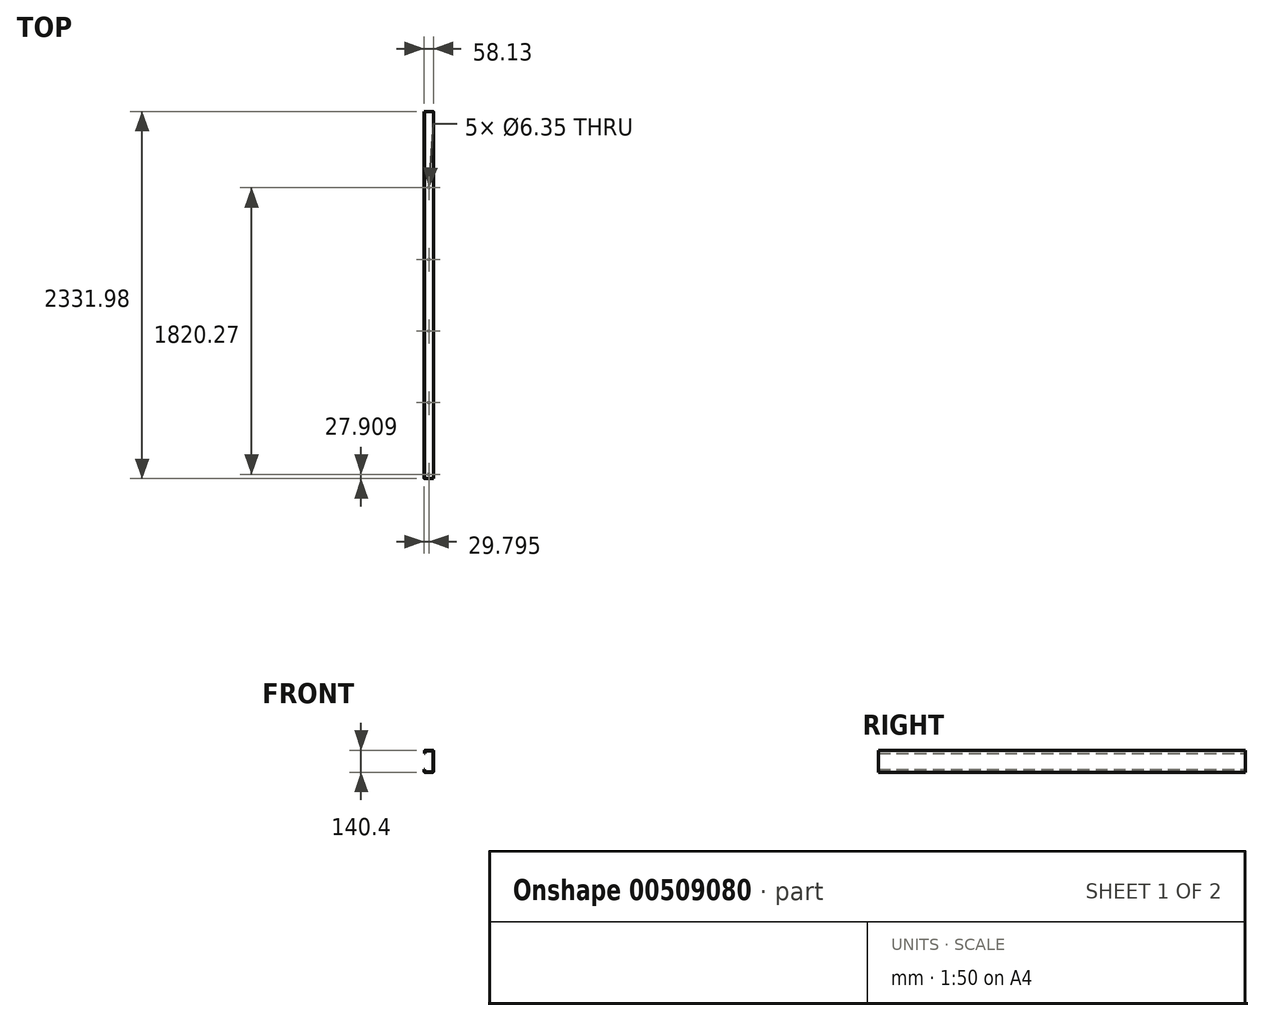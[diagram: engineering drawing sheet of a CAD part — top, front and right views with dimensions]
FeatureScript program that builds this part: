
annotation { "Feature Type Name" : "Feature", "Feature Type Description" : "" }
export const myFeature = defineFeature(function(context is Context, id is Id, definition is map)
    precondition{}
    {
        {
            var Q0;
            Q0=qCreatedBy(makeId("Front.planeOp"),FACE);
            var sketch = newSketch(context, id + "F0", { "sketchPlane" : qUnion([Q0])});
            skLineSegment(sketch, "E0", {"start": v(-431.8, -558.8) * mm, "end": v(431.8, -558.8) * mm});
            skLineSegment(sketch, "E1", {"start": v(431.8, -558.8) * mm, "end": v(431.8, 558.8) * mm});
            skLineSegment(sketch, "E2", {"start": v(431.8, 558.8) * mm, "end": v(-431.8, 558.8) * mm});
            skLineSegment(sketch, "E3", {"start": v(-431.8, 558.8) * mm, "end": v(-431.8, -558.8) * mm});
            skLineSegment(sketch, "E4", {"start": v(-381, -504.83) * mm, "end": v(381, -504.83) * mm});
            skLineSegment(sketch, "E5", {"start": v(381, -504.83) * mm, "end": v(381, 504.83) * mm});
            skLineSegment(sketch, "E6", {"start": v(381, 504.83) * mm, "end": v(360.7, 504.83) * mm});
            skLineSegment(sketch, "E7", {"start": v(265.82, 504.83) * mm, "end": v(-381, 504.83) * mm});
            skLineSegment(sketch, "E8", {"start": v(-381, 504.83) * mm, "end": v(-381, -504.83) * mm});
            skLineSegment(sketch, "E9", {"start": v(-381, -403.23) * mm, "end": v(381, -403.23) * mm});
            skLineSegment(sketch, "E10", {"start": v(-152.4, -403.23) * mm, "end": v(-152.4, -504.83) * mm});
            skLineSegment(sketch, "E11", {"start": v(152.4, -403.23) * mm, "end": v(152.4, -504.83) * mm});
            skLineSegment(sketch, "E12", {"start": v(349.12, 503.33) * mm, "end": v(324.77, 544.8) * mm});
            skLineSegment(sketch, "E13", {"start": v(324.92, 525.17) * mm, "end": v(343.26, 493.25) * mm});
            skLineSegment(sketch, "E14", {"start": v(345.3, 496.77) * mm, "end": v(323.11, 534.57) * mm});
            skLineSegment(sketch, "E15", {"start": v(351.17, 506.85) * mm, "end": v(327.06, 548.5) * mm});
            skLineSegment(sketch, "E16", {"start": v(335.24, 486.66) * mm, "end": v(339.43, 486.66) * mm});
            skLineSegment(sketch, "E17", {"start": v(323.53, 514.34) * mm, "end": v(339.43, 486.66) * mm});
            skLineSegment(sketch, "E18", {"start": v(324.77, 544.8) * mm, "end": v(303.2, 507.27) * mm});
            skLineSegment(sketch, "E19", {"start": v(323.11, 534.57) * mm, "end": v(305.2, 503.47) * mm});
            skLineSegment(sketch, "E20", {"start": v(303.02, 548.5) * mm, "end": v(279.32, 507.27) * mm});
            skLineSegment(sketch, "E21", {"start": v(305.2, 503.47) * mm, "end": v(281.51, 503.47) * mm});
            skLineSegment(sketch, "E22", {"start": v(303.2, 507.27) * mm, "end": v(279.32, 507.27) * mm});
            skLineSegment(sketch, "E23", {"start": v(287.46, 493.17) * mm, "end": v(311.53, 493.17) * mm});
            skLineSegment(sketch, "E24", {"start": v(285.48, 496.6) * mm, "end": v(309, 496.6) * mm});
            skLineSegment(sketch, "E25", {"start": v(315.3, 486.66) * mm, "end": v(291.22, 486.66) * mm});
            skLineSegment(sketch, "E26", {"start": v(281.51, 503.47) * mm, "end": v(285.48, 496.6) * mm});
            skLineSegment(sketch, "E27", {"start": v(287.46, 493.17) * mm, "end": v(291.22, 486.66) * mm});
            skLineSegment(sketch, "E28", {"start": v(309, 496.6) * mm, "end": v(324.92, 525.17) * mm});
            skLineSegment(sketch, "E29", {"start": v(311.53, 493.17) * mm, "end": v(323.53, 514.34) * mm});
            skLineSegment(sketch, "E30", {"start": v(325.28, 503.65) * mm, "end": v(315.3, 486.66) * mm});
            skLineSegment(sketch, "E31", {"start": v(319.7, 486.66) * mm, "end": v(326.89, 486.66) * mm});
            skLineSegment(sketch, "E32", {"start": v(319.7, 486.66) * mm, "end": v(323.3, 492.99) * mm});
            skLineSegment(sketch, "E33", {"start": v(335.24, 486.66) * mm, "end": v(325.28, 503.65) * mm});
            skLineSegment(sketch, "E34", {"start": v(323.3, 492.99) * mm, "end": v(326.89, 486.66) * mm});
            skLineSegment(sketch, "E35", {"start": v(327.06, 548.5) * mm, "end": v(303.02, 548.5) * mm});
            skLineSegment(sketch, "E36", {"start": v(343.26, 493.25) * mm, "end": v(345.3, 496.77) * mm});
            skLineSegment(sketch, "E37", {"start": v(349.12, 503.33) * mm, "end": v(351.17, 506.85) * mm});
            skCircle(sketch, "E38", {"center": v(350.6, 458.79) * mm, "radius": 1.85 * mm});
            skLineSegment(sketch, "E39", {"start": v(-201.65, 389.86) * mm, "end": v(-204.7, 389.86) * mm});
            skLineSegment(sketch, "E40", {"start": v(-201.65, 287.56) * mm, "end": v(-204.7, 287.56) * mm});
            skLineSegment(sketch, "E41", {"start": v(-204.7, 389.86) * mm, "end": v(-204.7, 405.1) * mm});
            skLineSegment(sketch, "E42", {"start": v(-201.65, 389.86) * mm, "end": v(-201.65, 405.1) * mm});
            skArc(sketch, "E43", {"start": v(-200.89, 405.86) * mm, "mid": v(-201.43, 405.64) * mm, "end": v(-201.65, 405.1) * mm});
            skArc(sketch, "E44", {"start": v(-200.89, 408.9) * mm, "mid": v(-203.58, 407.8) * mm, "end": v(-204.7, 405.1) * mm});
            skLineSegment(sketch, "E45", {"start": v(-200.89, 408.9) * mm, "end": v(-151.83, 408.9) * mm});
            skLineSegment(sketch, "E46", {"start": v(-200.89, 405.86) * mm, "end": v(-151.83, 405.86) * mm});
            skArc(sketch, "E47", {"start": v(-151.07, 405.1) * mm, "mid": v(-151.3, 405.64) * mm, "end": v(-151.83, 405.86) * mm});
            skArc(sketch, "E48", {"start": v(-148.02, 405.1) * mm, "mid": v(-149.14, 407.8) * mm, "end": v(-151.83, 408.9) * mm});
            skLineSegment(sketch, "E49", {"start": v(-148.02, 405.1) * mm, "end": v(-148.02, 272.32) * mm});
            skLineSegment(sketch, "E50", {"start": v(-151.07, 405.1) * mm, "end": v(-151.07, 272.32) * mm});
            skLineSegment(sketch, "E51", {"start": v(-204.7, 287.56) * mm, "end": v(-204.7, 273.15) * mm});
            skLineSegment(sketch, "E52", {"start": v(-201.65, 287.56) * mm, "end": v(-201.65, 273.15) * mm});
            skLineSegment(sketch, "E53", {"start": v(-200.06, 268.51) * mm, "end": v(-151.83, 268.51) * mm});
            skLineSegment(sketch, "E54", {"start": v(-200.06, 271.56) * mm, "end": v(-151.83, 271.56) * mm});
            skArc(sketch, "E55", {"start": v(-151.83, 271.56) * mm, "mid": v(-151.3, 271.79) * mm, "end": v(-151.07, 272.32) * mm});
            skArc(sketch, "E56", {"start": v(-151.83, 268.51) * mm, "mid": v(-149.14, 269.63) * mm, "end": v(-148.02, 272.32) * mm});
            skArc(sketch, "E57", {"start": v(-201.65, 273.15) * mm, "mid": v(-201.19, 272.03) * mm, "end": v(-200.06, 271.56) * mm});
            skArc(sketch, "E58", {"start": v(-204.7, 273.15) * mm, "mid": v(-203.34, 269.87) * mm, "end": v(-200.06, 268.51) * mm});
            skLineSegment(sketch, "E59", {"start": v(268.24, 192.18) * mm, "end": v(-275.4, 192.18) * mm});
            skLineSegment(sketch, "E60", {"start": v(-275.4, 267.58) * mm, "end": v(268.24, 267.58) * mm});
            skLineSegment(sketch, "E61", {"start": v(-275.4, 191.38) * mm, "end": v(268.24, 191.38) * mm});
            skLineSegment(sketch, "E62", {"start": v(-275.4, 189.56) * mm, "end": v(-275.4, 233.5) * mm});
            skLineSegment(sketch, "E63", {"start": v(-275.4, 238.46) * mm, "end": v(-275.4, 270.12) * mm});
            skLineSegment(sketch, "E64", {"start": v(-275.4, 233.5) * mm, "end": v(-264.27, 236) * mm});
            skLineSegment(sketch, "E65", {"start": v(-287.59, 236) * mm, "end": v(-275.4, 238.46) * mm});
            skLineSegment(sketch, "E66", {"start": v(-287.59, 236) * mm, "end": v(-264.27, 236) * mm});
            skLineSegment(sketch, "E67", {"start": v(268.24, 189.56) * mm, "end": v(268.24, 233.5) * mm});
            skLineSegment(sketch, "E68", {"start": v(268.24, 238.46) * mm, "end": v(268.24, 270.12) * mm});
            skLineSegment(sketch, "E69", {"start": v(268.24, 233.5) * mm, "end": v(279.38, 236) * mm});
            skLineSegment(sketch, "E70", {"start": v(256.06, 236) * mm, "end": v(268.24, 238.46) * mm});
            skLineSegment(sketch, "E71", {"start": v(256.06, 236) * mm, "end": v(279.38, 236) * mm});
            skLineSegment(sketch, "E72", {"start": v(267.92, 175.66) * mm, "end": v(267.92, 187.92) * mm});
            skLineSegment(sketch, "E73", {"start": v(-275.4, 175.66) * mm, "end": v(-275.4, 187.92) * mm});
            skLineSegment(sketch, "E74", {"start": v(131.2, 389.86) * mm, "end": v(128.15, 389.86) * mm});
            skLineSegment(sketch, "E75", {"start": v(131.2, 287.54) * mm, "end": v(128.15, 287.54) * mm});
            skLineSegment(sketch, "E76", {"start": v(128.15, 389.86) * mm, "end": v(128.15, 405.1) * mm});
            skLineSegment(sketch, "E77", {"start": v(131.2, 389.86) * mm, "end": v(131.2, 405.1) * mm});
            skArc(sketch, "E78", {"start": v(131.96, 408.9) * mm, "mid": v(129.27, 407.8) * mm, "end": v(128.15, 405.1) * mm});
            skLineSegment(sketch, "E79", {"start": v(131.96, 408.9) * mm, "end": v(182.96, 408.9) * mm});
            skLineSegment(sketch, "E80", {"start": v(131.96, 405.86) * mm, "end": v(182.96, 405.86) * mm});
            skArc(sketch, "E81", {"start": v(183.72, 405.1) * mm, "mid": v(183.5, 405.64) * mm, "end": v(182.96, 405.86) * mm});
            skArc(sketch, "E82", {"start": v(186.77, 405.1) * mm, "mid": v(185.65, 407.8) * mm, "end": v(182.96, 408.9) * mm});
            skLineSegment(sketch, "E83", {"start": v(186.77, 405.1) * mm, "end": v(186.77, 272.3) * mm});
            skLineSegment(sketch, "E84", {"start": v(183.72, 405.1) * mm, "end": v(183.72, 272.3) * mm});
            skLineSegment(sketch, "E85", {"start": v(128.15, 287.54) * mm, "end": v(128.15, 273.12) * mm});
            skLineSegment(sketch, "E86", {"start": v(131.2, 287.54) * mm, "end": v(131.2, 273.12) * mm});
            skLineSegment(sketch, "E87", {"start": v(132.79, 268.49) * mm, "end": v(182.96, 268.49) * mm});
            skLineSegment(sketch, "E88", {"start": v(132.79, 271.53) * mm, "end": v(182.96, 271.53) * mm});
            skArc(sketch, "E89", {"start": v(182.96, 271.53) * mm, "mid": v(183.5, 271.76) * mm, "end": v(183.72, 272.3) * mm});
            skArc(sketch, "E90", {"start": v(182.96, 268.49) * mm, "mid": v(185.65, 269.6) * mm, "end": v(186.77, 272.3) * mm});
            skArc(sketch, "E91", {"start": v(131.2, 273.12) * mm, "mid": v(131.67, 272) * mm, "end": v(132.79, 271.53) * mm});
            skArc(sketch, "E92", {"start": v(128.15, 273.12) * mm, "mid": v(129.51, 269.84) * mm, "end": v(132.79, 268.49) * mm});
            skLineSegment(sketch, "E93", {"start": v(-275.4, 266.78) * mm, "end": v(268.24, 266.78) * mm});
            skArc(sketch, "E94", {"start": v(131.96, 405.86) * mm, "mid": v(131.42, 405.64) * mm, "end": v(131.2, 405.1) * mm});
            skLineSegment(sketch, "E95", {"start": v(-148.02, 350.55) * mm, "end": v(-147.38, 350.55) * mm});
            skLineSegment(sketch, "E96", {"start": v(268.24, 220.63) * mm, "end": v(-275.4, 220.63) * mm});
            skLineSegment(sketch, "E97", {"start": v(-275.4, 219.83) * mm, "end": v(268.24, 219.83) * mm});
            skLineSegment(sketch, "E98", {"start": v(111.4, 219.88) * mm, "end": v(200.2, 219.88) * mm});
            skLineSegment(sketch, "E99", {"start": v(200.2, 219.88) * mm, "end": v(200.2, 218.1) * mm});
            skLineSegment(sketch, "E100", {"start": v(111.4, 219.88) * mm, "end": v(111.4, 218.1) * mm});
            skLineSegment(sketch, "E101", {"start": v(111.4, 218.1) * mm, "end": v(200.2, 218.1) * mm});
            skLineSegment(sketch, "E102", {"start": v(165.87, 216.24) * mm, "end": v(165.87, 217.5) * mm});
            skLineSegment(sketch, "E103", {"start": v(152.66, 216.24) * mm, "end": v(152.66, 217.5) * mm});
            skLineSegment(sketch, "E104", {"start": v(164.46, 211.81) * mm, "end": v(164.46, 216.24) * mm});
            skLineSegment(sketch, "E105", {"start": v(154.07, 211.81) * mm, "end": v(154.07, 216.24) * mm});
            skLineSegment(sketch, "E106", {"start": v(161.7, 259.32) * mm, "end": v(161.7, 260.34) * mm});
            skLineSegment(sketch, "E107", {"start": v(161.7, 261.14) * mm, "end": v(161.7, 262.16) * mm});
            skLineSegment(sketch, "E108", {"start": v(161.7, 262.95) * mm, "end": v(161.7, 263.97) * mm});
            skLineSegment(sketch, "E109", {"start": v(161.7, 264.76) * mm, "end": v(161.7, 265.78) * mm});
            skLineSegment(sketch, "E110", {"start": v(161.7, 266.58) * mm, "end": v(161.7, 267.6) * mm});
            skLineSegment(sketch, "E111", {"start": v(161.7, 268.39) * mm, "end": v(161.7, 269.41) * mm});
            skLineSegment(sketch, "E112", {"start": v(161.7, 270.2) * mm, "end": v(161.7, 271.22) * mm});
            skLineSegment(sketch, "E113", {"start": v(161.7, 272.02) * mm, "end": v(161.7, 273.04) * mm});
            skLineSegment(sketch, "E114", {"start": v(161.7, 273.83) * mm, "end": v(161.7, 274.85) * mm});
            skLineSegment(sketch, "E115", {"start": v(161.7, 275.64) * mm, "end": v(161.7, 276.67) * mm});
            skLineSegment(sketch, "E116", {"start": v(161.7, 277.46) * mm, "end": v(161.7, 278.48) * mm});
            skLineSegment(sketch, "E117", {"start": v(156.83, 257.5) * mm, "end": v(156.83, 258.53) * mm});
            skLineSegment(sketch, "E118", {"start": v(156.83, 259.32) * mm, "end": v(156.83, 260.34) * mm});
            skLineSegment(sketch, "E119", {"start": v(156.83, 261.14) * mm, "end": v(156.83, 262.16) * mm});
            skLineSegment(sketch, "E120", {"start": v(156.83, 262.95) * mm, "end": v(156.83, 263.97) * mm});
            skLineSegment(sketch, "E121", {"start": v(156.83, 264.76) * mm, "end": v(156.83, 265.78) * mm});
            skLineSegment(sketch, "E122", {"start": v(156.83, 266.58) * mm, "end": v(156.83, 267.6) * mm});
            skLineSegment(sketch, "E123", {"start": v(156.83, 268.39) * mm, "end": v(156.83, 269.41) * mm});
            skLineSegment(sketch, "E124", {"start": v(156.83, 270.2) * mm, "end": v(156.83, 271.22) * mm});
            skLineSegment(sketch, "E125", {"start": v(156.83, 272.02) * mm, "end": v(156.83, 273.04) * mm});
            skLineSegment(sketch, "E126", {"start": v(156.83, 273.83) * mm, "end": v(156.83, 274.85) * mm});
            skLineSegment(sketch, "E127", {"start": v(156.83, 275.64) * mm, "end": v(156.83, 276.67) * mm});
            skLineSegment(sketch, "E128", {"start": v(156.14, 258.93) * mm, "end": v(156.83, 258.53) * mm});
            skLineSegment(sketch, "E129", {"start": v(156.14, 258.93) * mm, "end": v(156.83, 259.32) * mm});
            skLineSegment(sketch, "E130", {"start": v(156.14, 260.74) * mm, "end": v(156.83, 260.34) * mm});
            skLineSegment(sketch, "E131", {"start": v(156.14, 260.74) * mm, "end": v(156.83, 261.14) * mm});
            skLineSegment(sketch, "E132", {"start": v(162.39, 260.74) * mm, "end": v(161.7, 260.34) * mm});
            skLineSegment(sketch, "E133", {"start": v(162.39, 260.74) * mm, "end": v(161.7, 261.14) * mm});
            skLineSegment(sketch, "E134", {"start": v(162.39, 262.55) * mm, "end": v(161.7, 262.16) * mm});
            skLineSegment(sketch, "E135", {"start": v(162.39, 262.55) * mm, "end": v(161.7, 262.95) * mm});
            skLineSegment(sketch, "E136", {"start": v(156.14, 258.93) * mm, "end": v(162.39, 260.74) * mm});
            skLineSegment(sketch, "E137", {"start": v(156.14, 260.74) * mm, "end": v(162.39, 262.55) * mm});
            skLineSegment(sketch, "E138", {"start": v(156.83, 258.53) * mm, "end": v(161.7, 260.34) * mm});
            skLineSegment(sketch, "E139", {"start": v(156.83, 259.32) * mm, "end": v(161.7, 261.14) * mm});
            skLineSegment(sketch, "E140", {"start": v(156.83, 260.34) * mm, "end": v(161.7, 262.16) * mm});
            skLineSegment(sketch, "E141", {"start": v(156.83, 261.14) * mm, "end": v(161.7, 262.95) * mm});
            skLineSegment(sketch, "E142", {"start": v(156.14, 262.55) * mm, "end": v(156.83, 262.16) * mm});
            skLineSegment(sketch, "E143", {"start": v(156.14, 262.55) * mm, "end": v(156.83, 262.95) * mm});
            skLineSegment(sketch, "E144", {"start": v(156.14, 264.37) * mm, "end": v(156.83, 263.97) * mm});
            skLineSegment(sketch, "E145", {"start": v(156.14, 264.37) * mm, "end": v(156.83, 264.76) * mm});
            skLineSegment(sketch, "E146", {"start": v(162.39, 264.37) * mm, "end": v(161.7, 263.97) * mm});
            skLineSegment(sketch, "E147", {"start": v(162.39, 264.37) * mm, "end": v(161.7, 264.76) * mm});
            skLineSegment(sketch, "E148", {"start": v(162.39, 266.18) * mm, "end": v(161.7, 265.78) * mm});
            skLineSegment(sketch, "E149", {"start": v(162.39, 266.18) * mm, "end": v(161.7, 266.58) * mm});
            skLineSegment(sketch, "E150", {"start": v(156.14, 262.55) * mm, "end": v(162.39, 264.37) * mm});
            skLineSegment(sketch, "E151", {"start": v(156.14, 264.37) * mm, "end": v(162.39, 266.18) * mm});
            skLineSegment(sketch, "E152", {"start": v(156.83, 262.16) * mm, "end": v(161.7, 263.97) * mm});
            skLineSegment(sketch, "E153", {"start": v(156.83, 262.95) * mm, "end": v(161.7, 264.76) * mm});
            skLineSegment(sketch, "E154", {"start": v(156.83, 263.97) * mm, "end": v(161.7, 265.78) * mm});
            skLineSegment(sketch, "E155", {"start": v(156.83, 264.76) * mm, "end": v(161.7, 266.58) * mm});
            skLineSegment(sketch, "E156", {"start": v(156.14, 266.18) * mm, "end": v(156.83, 265.78) * mm});
            skLineSegment(sketch, "E157", {"start": v(156.14, 266.18) * mm, "end": v(156.83, 266.58) * mm});
            skLineSegment(sketch, "E158", {"start": v(162.39, 268) * mm, "end": v(161.7, 267.6) * mm});
            skLineSegment(sketch, "E159", {"start": v(162.39, 268) * mm, "end": v(161.7, 268.39) * mm});
            skLineSegment(sketch, "E160", {"start": v(156.14, 266.18) * mm, "end": v(162.39, 268) * mm});
            skLineSegment(sketch, "E161", {"start": v(156.83, 265.78) * mm, "end": v(161.7, 267.6) * mm});
            skLineSegment(sketch, "E162", {"start": v(156.83, 266.58) * mm, "end": v(161.7, 268.39) * mm});
            skLineSegment(sketch, "E163", {"start": v(156.14, 268) * mm, "end": v(156.83, 267.6) * mm});
            skLineSegment(sketch, "E164", {"start": v(156.14, 268) * mm, "end": v(156.83, 268.39) * mm});
            skLineSegment(sketch, "E165", {"start": v(156.14, 269.8) * mm, "end": v(156.83, 269.41) * mm});
            skLineSegment(sketch, "E166", {"start": v(156.14, 269.8) * mm, "end": v(156.83, 270.2) * mm});
            skLineSegment(sketch, "E167", {"start": v(162.39, 269.8) * mm, "end": v(161.7, 269.41) * mm});
            skLineSegment(sketch, "E168", {"start": v(162.39, 269.8) * mm, "end": v(161.7, 270.2) * mm});
            skLineSegment(sketch, "E169", {"start": v(162.39, 271.62) * mm, "end": v(161.7, 271.22) * mm});
            skLineSegment(sketch, "E170", {"start": v(162.39, 271.62) * mm, "end": v(161.7, 272.02) * mm});
            skLineSegment(sketch, "E171", {"start": v(156.14, 268) * mm, "end": v(162.39, 269.8) * mm});
            skLineSegment(sketch, "E172", {"start": v(156.14, 269.8) * mm, "end": v(162.39, 271.62) * mm});
            skLineSegment(sketch, "E173", {"start": v(156.83, 267.6) * mm, "end": v(161.7, 269.41) * mm});
            skLineSegment(sketch, "E174", {"start": v(156.83, 268.39) * mm, "end": v(161.7, 270.2) * mm});
            skLineSegment(sketch, "E175", {"start": v(156.83, 269.41) * mm, "end": v(161.7, 271.22) * mm});
            skLineSegment(sketch, "E176", {"start": v(156.83, 270.2) * mm, "end": v(161.7, 272.02) * mm});
            skLineSegment(sketch, "E177", {"start": v(156.14, 271.62) * mm, "end": v(156.83, 271.22) * mm});
            skLineSegment(sketch, "E178", {"start": v(156.14, 271.62) * mm, "end": v(156.83, 272.02) * mm});
            skLineSegment(sketch, "E179", {"start": v(156.14, 273.43) * mm, "end": v(156.83, 273.04) * mm});
            skLineSegment(sketch, "E180", {"start": v(156.14, 273.43) * mm, "end": v(156.83, 273.83) * mm});
            skLineSegment(sketch, "E181", {"start": v(162.39, 273.43) * mm, "end": v(161.7, 273.04) * mm});
            skLineSegment(sketch, "E182", {"start": v(162.39, 273.43) * mm, "end": v(161.7, 273.83) * mm});
            skLineSegment(sketch, "E183", {"start": v(162.39, 275.25) * mm, "end": v(161.7, 274.85) * mm});
            skLineSegment(sketch, "E184", {"start": v(162.39, 275.25) * mm, "end": v(161.7, 275.64) * mm});
            skLineSegment(sketch, "E185", {"start": v(156.14, 271.62) * mm, "end": v(162.39, 273.43) * mm});
            skLineSegment(sketch, "E186", {"start": v(156.14, 273.43) * mm, "end": v(162.39, 275.25) * mm});
            skLineSegment(sketch, "E187", {"start": v(156.83, 271.22) * mm, "end": v(161.7, 273.04) * mm});
            skLineSegment(sketch, "E188", {"start": v(156.83, 272.02) * mm, "end": v(161.7, 273.83) * mm});
            skLineSegment(sketch, "E189", {"start": v(156.83, 273.04) * mm, "end": v(161.7, 274.85) * mm});
            skLineSegment(sketch, "E190", {"start": v(156.83, 273.83) * mm, "end": v(161.7, 275.64) * mm});
            skLineSegment(sketch, "E191", {"start": v(156.14, 275.25) * mm, "end": v(156.83, 274.85) * mm});
            skLineSegment(sketch, "E192", {"start": v(156.14, 275.25) * mm, "end": v(156.83, 275.64) * mm});
            skLineSegment(sketch, "E193", {"start": v(156.14, 277.06) * mm, "end": v(156.83, 276.67) * mm});
            skLineSegment(sketch, "E194", {"start": v(156.14, 277.06) * mm, "end": v(156.83, 277.46) * mm});
            skLineSegment(sketch, "E195", {"start": v(162.39, 277.06) * mm, "end": v(161.7, 276.67) * mm});
            skLineSegment(sketch, "E196", {"start": v(162.39, 277.06) * mm, "end": v(161.7, 277.46) * mm});
            skLineSegment(sketch, "E197", {"start": v(162.39, 278.87) * mm, "end": v(161.7, 278.48) * mm});
            skLineSegment(sketch, "E198", {"start": v(162.39, 278.87) * mm, "end": v(161.7, 279.27) * mm});
            skLineSegment(sketch, "E199", {"start": v(156.14, 275.25) * mm, "end": v(162.39, 277.06) * mm});
            skLineSegment(sketch, "E200", {"start": v(156.14, 277.06) * mm, "end": v(162.39, 278.87) * mm});
            skLineSegment(sketch, "E201", {"start": v(156.83, 274.85) * mm, "end": v(161.7, 276.67) * mm});
            skLineSegment(sketch, "E202", {"start": v(156.83, 275.64) * mm, "end": v(161.7, 277.46) * mm});
            skLineSegment(sketch, "E203", {"start": v(156.83, 276.67) * mm, "end": v(161.7, 278.48) * mm});
            skLineSegment(sketch, "E204", {"start": v(156.83, 277.46) * mm, "end": v(161.7, 279.27) * mm});
            skLineSegment(sketch, "E205", {"start": v(152.66, 217.5) * mm, "end": v(165.87, 217.5) * mm});
            skLineSegment(sketch, "E206", {"start": v(152.66, 216.24) * mm, "end": v(165.87, 216.24) * mm});
            skLineSegment(sketch, "E207", {"start": v(154.77, 211.41) * mm, "end": v(163.76, 211.41) * mm});
            skLineSegment(sketch, "E208", {"start": v(156.67, 211.81) * mm, "end": v(156.67, 216.24) * mm});
            skLineSegment(sketch, "E209", {"start": v(161.86, 211.81) * mm, "end": v(161.86, 216.24) * mm});
            skLineSegment(sketch, "E210", {"start": v(154.77, 211.41) * mm, "end": v(154.07, 211.81) * mm});
            skLineSegment(sketch, "E211", {"start": v(163.76, 211.41) * mm, "end": v(164.46, 211.81) * mm});
            skLineSegment(sketch, "E212", {"start": v(161.16, 211.41) * mm, "end": v(161.86, 211.81) * mm});
            skLineSegment(sketch, "E213", {"start": v(155.97, 211.41) * mm, "end": v(156.67, 211.81) * mm});
            skLineSegment(sketch, "E214", {"start": v(162.56, 211.41) * mm, "end": v(161.86, 211.81) * mm});
            skLineSegment(sketch, "E215", {"start": v(157.36, 211.41) * mm, "end": v(156.67, 211.81) * mm});
            skLineSegment(sketch, "E216", {"start": v(156.83, 277.46) * mm, "end": v(156.83, 288.94) * mm});
            skLineSegment(sketch, "E217", {"start": v(161.05, 279.03) * mm, "end": v(161.05, 288.94) * mm});
            skLineSegment(sketch, "E218", {"start": v(158.94, 290.16) * mm, "end": v(156.83, 288.94) * mm});
            skLineSegment(sketch, "E219", {"start": v(158.94, 290.16) * mm, "end": v(161.05, 288.94) * mm});
            skLineSegment(sketch, "E220", {"start": v(158.94, 290.16) * mm, "end": v(158.94, 280.63) * mm});
            skArc(sketch, "E221", {"start": v(158.94, 280.63) * mm, "mid": v(159.28, 279.49) * mm, "end": v(160.18, 278.7) * mm});
            skLineSegment(sketch, "E222", {"start": v(156.14, 257.11) * mm, "end": v(156.83, 256.72) * mm});
            skLineSegment(sketch, "E223", {"start": v(156.14, 257.11) * mm, "end": v(156.83, 257.5) * mm});
            skLineSegment(sketch, "E224", {"start": v(162.39, 258.93) * mm, "end": v(161.7, 258.53) * mm});
            skLineSegment(sketch, "E225", {"start": v(162.39, 258.93) * mm, "end": v(161.7, 259.32) * mm});
            skLineSegment(sketch, "E226", {"start": v(156.14, 257.11) * mm, "end": v(162.39, 258.93) * mm});
            skLineSegment(sketch, "E227", {"start": v(156.83, 256.72) * mm, "end": v(161.7, 258.53) * mm});
            skLineSegment(sketch, "E228", {"start": v(156.83, 257.5) * mm, "end": v(161.7, 259.32) * mm});
            skLineSegment(sketch, "E229", {"start": v(156.83, 256.72) * mm, "end": v(156.83, 217.5) * mm});
            skLineSegment(sketch, "E230", {"start": v(161.7, 258.53) * mm, "end": v(161.7, 217.5) * mm});
            skLineSegment(sketch, "E231", {"start": v(-224.84, 219.88) * mm, "end": v(-136.05, 219.88) * mm});
            skLineSegment(sketch, "E232", {"start": v(-224.84, 218.1) * mm, "end": v(-136.05, 218.1) * mm});
            skLineSegment(sketch, "E233", {"start": v(-136.05, 219.88) * mm, "end": v(-136.05, 218.1) * mm});
            skLineSegment(sketch, "E234", {"start": v(-224.84, 219.88) * mm, "end": v(-224.84, 218.1) * mm});
            skLineSegment(sketch, "E235", {"start": v(-170.37, 216.24) * mm, "end": v(-170.37, 217.5) * mm});
            skLineSegment(sketch, "E236", {"start": v(-183.58, 216.24) * mm, "end": v(-183.58, 217.5) * mm});
            skLineSegment(sketch, "E237", {"start": v(-171.78, 211.81) * mm, "end": v(-171.78, 216.24) * mm});
            skLineSegment(sketch, "E238", {"start": v(-182.17, 211.81) * mm, "end": v(-182.17, 216.24) * mm});
            skLineSegment(sketch, "E239", {"start": v(-174.54, 259.32) * mm, "end": v(-174.54, 260.34) * mm});
            skLineSegment(sketch, "E240", {"start": v(-174.54, 261.14) * mm, "end": v(-174.54, 262.16) * mm});
            skLineSegment(sketch, "E241", {"start": v(-174.54, 262.95) * mm, "end": v(-174.54, 263.97) * mm});
            skLineSegment(sketch, "E242", {"start": v(-174.54, 264.76) * mm, "end": v(-174.54, 265.78) * mm});
            skLineSegment(sketch, "E243", {"start": v(-174.54, 266.58) * mm, "end": v(-174.54, 267.6) * mm});
            skLineSegment(sketch, "E244", {"start": v(-174.54, 268.39) * mm, "end": v(-174.54, 269.41) * mm});
            skLineSegment(sketch, "E245", {"start": v(-174.54, 270.2) * mm, "end": v(-174.54, 271.22) * mm});
            skLineSegment(sketch, "E246", {"start": v(-174.54, 272.02) * mm, "end": v(-174.54, 273.04) * mm});
            skLineSegment(sketch, "E247", {"start": v(-174.54, 273.83) * mm, "end": v(-174.54, 274.85) * mm});
            skLineSegment(sketch, "E248", {"start": v(-174.54, 275.64) * mm, "end": v(-174.54, 276.67) * mm});
            skLineSegment(sketch, "E249", {"start": v(-174.54, 277.46) * mm, "end": v(-174.54, 278.48) * mm});
            skLineSegment(sketch, "E250", {"start": v(-179.41, 257.5) * mm, "end": v(-179.41, 258.53) * mm});
            skLineSegment(sketch, "E251", {"start": v(-179.41, 259.32) * mm, "end": v(-179.41, 260.34) * mm});
            skLineSegment(sketch, "E252", {"start": v(-179.41, 261.14) * mm, "end": v(-179.41, 262.16) * mm});
            skLineSegment(sketch, "E253", {"start": v(-179.41, 262.95) * mm, "end": v(-179.41, 263.97) * mm});
            skLineSegment(sketch, "E254", {"start": v(-179.41, 264.76) * mm, "end": v(-179.41, 265.78) * mm});
            skLineSegment(sketch, "E255", {"start": v(-179.41, 266.58) * mm, "end": v(-179.41, 267.6) * mm});
            skLineSegment(sketch, "E256", {"start": v(-179.41, 268.39) * mm, "end": v(-179.41, 269.41) * mm});
            skLineSegment(sketch, "E257", {"start": v(-179.41, 270.2) * mm, "end": v(-179.41, 271.22) * mm});
            skLineSegment(sketch, "E258", {"start": v(-179.41, 272.02) * mm, "end": v(-179.41, 273.04) * mm});
            skLineSegment(sketch, "E259", {"start": v(-179.41, 273.83) * mm, "end": v(-179.41, 274.85) * mm});
            skLineSegment(sketch, "E260", {"start": v(-179.41, 275.64) * mm, "end": v(-179.41, 276.67) * mm});
            skLineSegment(sketch, "E261", {"start": v(-180.1, 258.93) * mm, "end": v(-179.41, 258.53) * mm});
            skLineSegment(sketch, "E262", {"start": v(-180.1, 258.93) * mm, "end": v(-179.41, 259.32) * mm});
            skLineSegment(sketch, "E263", {"start": v(-180.1, 260.74) * mm, "end": v(-179.41, 260.34) * mm});
            skLineSegment(sketch, "E264", {"start": v(-180.1, 260.74) * mm, "end": v(-179.41, 261.14) * mm});
            skLineSegment(sketch, "E265", {"start": v(-173.85, 260.74) * mm, "end": v(-174.54, 260.34) * mm});
            skLineSegment(sketch, "E266", {"start": v(-173.85, 260.74) * mm, "end": v(-174.54, 261.14) * mm});
            skLineSegment(sketch, "E267", {"start": v(-173.85, 262.55) * mm, "end": v(-174.54, 262.16) * mm});
            skLineSegment(sketch, "E268", {"start": v(-173.85, 262.55) * mm, "end": v(-174.54, 262.95) * mm});
            skLineSegment(sketch, "E269", {"start": v(-180.1, 258.93) * mm, "end": v(-173.85, 260.74) * mm});
            skLineSegment(sketch, "E270", {"start": v(-180.1, 260.74) * mm, "end": v(-173.85, 262.55) * mm});
            skLineSegment(sketch, "E271", {"start": v(-179.41, 258.53) * mm, "end": v(-174.54, 260.34) * mm});
            skLineSegment(sketch, "E272", {"start": v(-179.41, 259.32) * mm, "end": v(-174.54, 261.14) * mm});
            skLineSegment(sketch, "E273", {"start": v(-179.41, 260.34) * mm, "end": v(-174.54, 262.16) * mm});
            skLineSegment(sketch, "E274", {"start": v(-179.41, 261.14) * mm, "end": v(-174.54, 262.95) * mm});
            skLineSegment(sketch, "E275", {"start": v(-180.1, 262.55) * mm, "end": v(-179.41, 262.16) * mm});
            skLineSegment(sketch, "E276", {"start": v(-180.1, 262.55) * mm, "end": v(-179.41, 262.95) * mm});
            skLineSegment(sketch, "E277", {"start": v(-180.1, 264.37) * mm, "end": v(-179.41, 263.97) * mm});
            skLineSegment(sketch, "E278", {"start": v(-180.1, 264.37) * mm, "end": v(-179.41, 264.76) * mm});
            skLineSegment(sketch, "E279", {"start": v(-173.85, 264.37) * mm, "end": v(-174.54, 263.97) * mm});
            skLineSegment(sketch, "E280", {"start": v(-173.85, 264.37) * mm, "end": v(-174.54, 264.76) * mm});
            skLineSegment(sketch, "E281", {"start": v(-173.85, 266.18) * mm, "end": v(-174.54, 265.78) * mm});
            skLineSegment(sketch, "E282", {"start": v(-173.85, 266.18) * mm, "end": v(-174.54, 266.58) * mm});
            skLineSegment(sketch, "E283", {"start": v(-180.1, 262.55) * mm, "end": v(-173.85, 264.37) * mm});
            skLineSegment(sketch, "E284", {"start": v(-180.1, 264.37) * mm, "end": v(-173.85, 266.18) * mm});
            skLineSegment(sketch, "E285", {"start": v(-179.41, 262.16) * mm, "end": v(-174.54, 263.97) * mm});
            skLineSegment(sketch, "E286", {"start": v(-179.41, 262.95) * mm, "end": v(-174.54, 264.76) * mm});
            skLineSegment(sketch, "E287", {"start": v(-179.41, 263.97) * mm, "end": v(-174.54, 265.78) * mm});
            skLineSegment(sketch, "E288", {"start": v(-179.41, 264.76) * mm, "end": v(-174.54, 266.58) * mm});
            skLineSegment(sketch, "E289", {"start": v(-180.1, 266.18) * mm, "end": v(-179.41, 265.78) * mm});
            skLineSegment(sketch, "E290", {"start": v(-180.1, 266.18) * mm, "end": v(-179.41, 266.58) * mm});
            skLineSegment(sketch, "E291", {"start": v(-173.85, 268) * mm, "end": v(-174.54, 267.6) * mm});
            skLineSegment(sketch, "E292", {"start": v(-173.85, 268) * mm, "end": v(-174.54, 268.39) * mm});
            skLineSegment(sketch, "E293", {"start": v(-180.1, 266.18) * mm, "end": v(-173.85, 268) * mm});
            skLineSegment(sketch, "E294", {"start": v(-179.41, 265.78) * mm, "end": v(-174.54, 267.6) * mm});
            skLineSegment(sketch, "E295", {"start": v(-179.41, 266.58) * mm, "end": v(-174.54, 268.39) * mm});
            skLineSegment(sketch, "E296", {"start": v(-180.1, 268) * mm, "end": v(-179.41, 267.6) * mm});
            skLineSegment(sketch, "E297", {"start": v(-180.1, 268) * mm, "end": v(-179.41, 268.39) * mm});
            skLineSegment(sketch, "E298", {"start": v(-180.1, 269.8) * mm, "end": v(-179.41, 269.41) * mm});
            skLineSegment(sketch, "E299", {"start": v(-180.1, 269.8) * mm, "end": v(-179.41, 270.2) * mm});
            skLineSegment(sketch, "E300", {"start": v(-173.85, 269.8) * mm, "end": v(-174.54, 269.41) * mm});
            skLineSegment(sketch, "E301", {"start": v(-173.85, 269.8) * mm, "end": v(-174.54, 270.2) * mm});
            skLineSegment(sketch, "E302", {"start": v(-173.85, 271.62) * mm, "end": v(-174.54, 271.22) * mm});
            skLineSegment(sketch, "E303", {"start": v(-173.85, 271.62) * mm, "end": v(-174.54, 272.02) * mm});
            skLineSegment(sketch, "E304", {"start": v(-180.1, 268) * mm, "end": v(-173.85, 269.8) * mm});
            skLineSegment(sketch, "E305", {"start": v(-180.1, 269.8) * mm, "end": v(-173.85, 271.62) * mm});
            skLineSegment(sketch, "E306", {"start": v(-179.41, 267.6) * mm, "end": v(-174.54, 269.41) * mm});
            skLineSegment(sketch, "E307", {"start": v(-179.41, 268.39) * mm, "end": v(-174.54, 270.2) * mm});
            skLineSegment(sketch, "E308", {"start": v(-179.41, 269.41) * mm, "end": v(-174.54, 271.22) * mm});
            skLineSegment(sketch, "E309", {"start": v(-179.41, 270.2) * mm, "end": v(-174.54, 272.02) * mm});
            skLineSegment(sketch, "E310", {"start": v(-180.1, 271.62) * mm, "end": v(-179.41, 271.22) * mm});
            skLineSegment(sketch, "E311", {"start": v(-180.1, 271.62) * mm, "end": v(-179.41, 272.02) * mm});
            skLineSegment(sketch, "E312", {"start": v(-180.1, 273.43) * mm, "end": v(-179.41, 273.04) * mm});
            skLineSegment(sketch, "E313", {"start": v(-180.1, 273.43) * mm, "end": v(-179.41, 273.83) * mm});
            skLineSegment(sketch, "E314", {"start": v(-173.85, 273.43) * mm, "end": v(-174.54, 273.04) * mm});
            skLineSegment(sketch, "E315", {"start": v(-173.85, 273.43) * mm, "end": v(-174.54, 273.83) * mm});
            skLineSegment(sketch, "E316", {"start": v(-173.85, 275.25) * mm, "end": v(-174.54, 274.85) * mm});
            skLineSegment(sketch, "E317", {"start": v(-173.85, 275.25) * mm, "end": v(-174.54, 275.64) * mm});
            skLineSegment(sketch, "E318", {"start": v(-180.1, 271.62) * mm, "end": v(-173.85, 273.43) * mm});
            skLineSegment(sketch, "E319", {"start": v(-180.1, 273.43) * mm, "end": v(-173.85, 275.25) * mm});
            skLineSegment(sketch, "E320", {"start": v(-179.41, 271.22) * mm, "end": v(-174.54, 273.04) * mm});
            skLineSegment(sketch, "E321", {"start": v(-179.41, 272.02) * mm, "end": v(-174.54, 273.83) * mm});
            skLineSegment(sketch, "E322", {"start": v(-179.41, 273.04) * mm, "end": v(-174.54, 274.85) * mm});
            skLineSegment(sketch, "E323", {"start": v(-179.41, 273.83) * mm, "end": v(-174.54, 275.64) * mm});
            skLineSegment(sketch, "E324", {"start": v(-180.1, 275.25) * mm, "end": v(-179.41, 274.85) * mm});
            skLineSegment(sketch, "E325", {"start": v(-180.1, 275.25) * mm, "end": v(-179.41, 275.64) * mm});
            skLineSegment(sketch, "E326", {"start": v(-180.1, 277.06) * mm, "end": v(-179.41, 276.67) * mm});
            skLineSegment(sketch, "E327", {"start": v(-180.1, 277.06) * mm, "end": v(-179.41, 277.46) * mm});
            skLineSegment(sketch, "E328", {"start": v(-173.85, 277.06) * mm, "end": v(-174.54, 276.67) * mm});
            skLineSegment(sketch, "E329", {"start": v(-173.85, 277.06) * mm, "end": v(-174.54, 277.46) * mm});
            skLineSegment(sketch, "E330", {"start": v(-173.85, 278.87) * mm, "end": v(-174.54, 278.48) * mm});
            skLineSegment(sketch, "E331", {"start": v(-173.85, 278.87) * mm, "end": v(-174.54, 279.27) * mm});
            skLineSegment(sketch, "E332", {"start": v(-180.1, 275.25) * mm, "end": v(-173.85, 277.06) * mm});
            skLineSegment(sketch, "E333", {"start": v(-180.1, 277.06) * mm, "end": v(-173.85, 278.87) * mm});
            skLineSegment(sketch, "E334", {"start": v(-179.41, 274.85) * mm, "end": v(-174.54, 276.67) * mm});
            skLineSegment(sketch, "E335", {"start": v(-179.41, 275.64) * mm, "end": v(-174.54, 277.46) * mm});
            skLineSegment(sketch, "E336", {"start": v(-179.41, 276.67) * mm, "end": v(-174.54, 278.48) * mm});
            skLineSegment(sketch, "E337", {"start": v(-179.41, 277.46) * mm, "end": v(-174.54, 279.27) * mm});
            skLineSegment(sketch, "E338", {"start": v(-183.58, 217.5) * mm, "end": v(-170.37, 217.5) * mm});
            skLineSegment(sketch, "E339", {"start": v(-183.58, 216.24) * mm, "end": v(-170.37, 216.24) * mm});
            skLineSegment(sketch, "E340", {"start": v(-181.47, 211.41) * mm, "end": v(-172.48, 211.41) * mm});
            skLineSegment(sketch, "E341", {"start": v(-179.57, 211.81) * mm, "end": v(-179.57, 216.24) * mm});
            skLineSegment(sketch, "E342", {"start": v(-174.38, 211.81) * mm, "end": v(-174.38, 216.24) * mm});
            skLineSegment(sketch, "E343", {"start": v(-181.47, 211.41) * mm, "end": v(-182.17, 211.81) * mm});
            skLineSegment(sketch, "E344", {"start": v(-172.48, 211.41) * mm, "end": v(-171.78, 211.81) * mm});
            skLineSegment(sketch, "E345", {"start": v(-175.07, 211.41) * mm, "end": v(-174.38, 211.81) * mm});
            skLineSegment(sketch, "E346", {"start": v(-180.27, 211.41) * mm, "end": v(-179.57, 211.81) * mm});
            skLineSegment(sketch, "E347", {"start": v(-173.68, 211.41) * mm, "end": v(-174.38, 211.81) * mm});
            skLineSegment(sketch, "E348", {"start": v(-178.88, 211.41) * mm, "end": v(-179.57, 211.81) * mm});
            skLineSegment(sketch, "E349", {"start": v(-179.41, 277.46) * mm, "end": v(-179.41, 288.94) * mm});
            skLineSegment(sketch, "E350", {"start": v(-175.19, 279.03) * mm, "end": v(-175.19, 288.94) * mm});
            skLineSegment(sketch, "E351", {"start": v(-177.3, 290.16) * mm, "end": v(-179.41, 288.94) * mm});
            skLineSegment(sketch, "E352", {"start": v(-177.3, 290.16) * mm, "end": v(-175.19, 288.94) * mm});
            skLineSegment(sketch, "E353", {"start": v(-177.3, 290.16) * mm, "end": v(-177.3, 280.63) * mm});
            skArc(sketch, "E354", {"start": v(-177.3, 280.63) * mm, "mid": v(-176.96, 279.49) * mm, "end": v(-176.05, 278.7) * mm});
            skLineSegment(sketch, "E355", {"start": v(-180.1, 257.11) * mm, "end": v(-179.41, 256.72) * mm});
            skLineSegment(sketch, "E356", {"start": v(-180.1, 257.11) * mm, "end": v(-179.41, 257.5) * mm});
            skLineSegment(sketch, "E357", {"start": v(-173.85, 258.93) * mm, "end": v(-174.54, 258.53) * mm});
            skLineSegment(sketch, "E358", {"start": v(-173.85, 258.93) * mm, "end": v(-174.54, 259.32) * mm});
            skLineSegment(sketch, "E359", {"start": v(-180.1, 257.11) * mm, "end": v(-173.85, 258.93) * mm});
            skLineSegment(sketch, "E360", {"start": v(-179.41, 256.72) * mm, "end": v(-174.54, 258.53) * mm});
            skLineSegment(sketch, "E361", {"start": v(-179.41, 257.5) * mm, "end": v(-174.54, 259.32) * mm});
            skLineSegment(sketch, "E362", {"start": v(-179.41, 256.72) * mm, "end": v(-179.41, 217.5) * mm});
            skLineSegment(sketch, "E363", {"start": v(-174.54, 258.53) * mm, "end": v(-174.54, 217.5) * mm});
            skLineSegment(sketch, "E364", {"start": v(-148.02, 412.03) * mm, "end": v(-148.02, 438.03) * mm});
            skLineSegment(sketch, "E365", {"start": v(187, 413.37) * mm, "end": v(187, 438.03) * mm});
            skLineSegment(sketch, "E366", {"start": v(-234.68, 434.85) * mm, "end": v(273.7, 434.85) * mm});
            skLineSegment(sketch, "E367", {"start": v(100.58, -60.7) * mm, "end": v(103.63, -60.7) * mm});
            skLineSegment(sketch, "E368", {"start": v(103.63, -60.7) * mm, "end": v(103.63, -75.11) * mm});
            skLineSegment(sketch, "E369", {"start": v(100.58, -60.7) * mm, "end": v(100.58, -75.11) * mm});
            skLineSegment(sketch, "E370", {"start": v(99, -79.75) * mm, "end": v(49, -79.75) * mm});
            skLineSegment(sketch, "E371", {"start": v(99, -76.7) * mm, "end": v(49, -76.7) * mm});
            skArc(sketch, "E372", {"start": v(48.23, -75.94) * mm, "mid": v(48.45, -76.48) * mm, "end": v(49, -76.7) * mm});
            skArc(sketch, "E373", {"start": v(45.18, -75.94) * mm, "mid": v(46.3, -78.63) * mm, "end": v(49, -79.75) * mm});
            skArc(sketch, "E374", {"start": v(99, -76.7) * mm, "mid": v(100.11, -76.23) * mm, "end": v(100.58, -75.11) * mm});
            skArc(sketch, "E375", {"start": v(99, -79.75) * mm, "mid": v(102.27, -78.39) * mm, "end": v(103.63, -75.11) * mm});
            skLineSegment(sketch, "E376", {"start": v(-10.55, -60.7) * mm, "end": v(-13.6, -60.7) * mm});
            skLineSegment(sketch, "E377", {"start": v(-13.6, -60.7) * mm, "end": v(-13.6, -75.11) * mm});
            skLineSegment(sketch, "E378", {"start": v(-10.55, -60.7) * mm, "end": v(-10.55, -75.11) * mm});
            skLineSegment(sketch, "E379", {"start": v(-8.96, -79.75) * mm, "end": v(40.73, -79.75) * mm});
            skLineSegment(sketch, "E380", {"start": v(-8.96, -76.7) * mm, "end": v(40.73, -76.7) * mm});
            skArc(sketch, "E381", {"start": v(40.73, -76.7) * mm, "mid": v(41.27, -76.48) * mm, "end": v(41.5, -75.94) * mm});
            skArc(sketch, "E382", {"start": v(40.73, -79.75) * mm, "mid": v(43.43, -78.63) * mm, "end": v(44.54, -75.94) * mm});
            skArc(sketch, "E383", {"start": v(-10.55, -75.11) * mm, "mid": v(-10.08, -76.23) * mm, "end": v(-8.96, -76.7) * mm});
            skArc(sketch, "E384", {"start": v(-13.6, -75.11) * mm, "mid": v(-12.24, -78.39) * mm, "end": v(-8.96, -79.75) * mm});
            skLineSegment(sketch, "E385", {"start": v(49.63, -162.09) * mm, "end": v(187.74, -162.09) * mm});
            skLineSegment(sketch, "E386", {"start": v(187.74, -86.69) * mm, "end": v(49.63, -86.69) * mm});
            skLineSegment(sketch, "E387", {"start": v(49.63, -87.49) * mm, "end": v(187.74, -87.49) * mm});
            skLineSegment(sketch, "E388", {"start": v(187.74, -162.89) * mm, "end": v(49.63, -162.89) * mm});
            skLineSegment(sketch, "E389", {"start": v(49.63, -162.89) * mm, "end": v(49.63, -86.69) * mm});
            skLineSegment(sketch, "E390", {"start": v(40.1, -162.09) * mm, "end": v(-105.22, -162.09) * mm});
            skLineSegment(sketch, "E391", {"start": v(-105.22, -86.69) * mm, "end": v(40.1, -86.69) * mm});
            skLineSegment(sketch, "E392", {"start": v(40.1, -87.49) * mm, "end": v(-105.22, -87.49) * mm});
            skLineSegment(sketch, "E393", {"start": v(-105.22, -162.89) * mm, "end": v(40.1, -162.89) * mm});
            skLineSegment(sketch, "E394", {"start": v(40.1, -162.89) * mm, "end": v(40.1, -86.69) * mm});
            skLineSegment(sketch, "E395", {"start": v(-105.22, -164.71) * mm, "end": v(-105.22, -120.76) * mm});
            skLineSegment(sketch, "E396", {"start": v(-105.22, -115.81) * mm, "end": v(-105.22, -84.15) * mm});
            skLineSegment(sketch, "E397", {"start": v(-105.22, -120.76) * mm, "end": v(-94.08, -118.26) * mm});
            skLineSegment(sketch, "E398", {"start": v(-117.4, -118.26) * mm, "end": v(-105.22, -115.81) * mm});
            skLineSegment(sketch, "E399", {"start": v(-117.4, -118.26) * mm, "end": v(-94.08, -118.26) * mm});
            skLineSegment(sketch, "E400", {"start": v(187.74, -164.71) * mm, "end": v(187.74, -120.76) * mm});
            skLineSegment(sketch, "E401", {"start": v(187.74, -115.81) * mm, "end": v(187.74, -84.15) * mm});
            skLineSegment(sketch, "E402", {"start": v(187.74, -120.76) * mm, "end": v(198.88, -118.26) * mm});
            skLineSegment(sketch, "E403", {"start": v(175.56, -118.26) * mm, "end": v(187.74, -115.81) * mm});
            skLineSegment(sketch, "E404", {"start": v(175.56, -118.26) * mm, "end": v(198.88, -118.26) * mm});
            skLineSegment(sketch, "E405", {"start": v(-19.05, -169.3) * mm, "end": v(108.77, -169.3) * mm});
            skLineSegment(sketch, "E406", {"start": v(-18.84, -167.77) * mm, "end": v(108.57, -167.77) * mm});
            skLineSegment(sketch, "E407", {"start": v(108.57, -167.77) * mm, "end": v(119.2, -164.92) * mm});
            skLineSegment(sketch, "E408", {"start": v(108.77, -169.3) * mm, "end": v(119.6, -166.4) * mm});
            skLineSegment(sketch, "E409", {"start": v(-18.84, -167.77) * mm, "end": v(-29.47, -164.92) * mm});
            skLineSegment(sketch, "E410", {"start": v(-19.05, -169.3) * mm, "end": v(-29.87, -166.4) * mm});
            skLineSegment(sketch, "E411", {"start": v(-18.84, -81.48) * mm, "end": v(108.56, -81.48) * mm});
            skLineSegment(sketch, "E412", {"start": v(-18.64, -83) * mm, "end": v(108.36, -83) * mm});
            skLineSegment(sketch, "E413", {"start": v(108.36, -83) * mm, "end": v(119.16, -83) * mm});
            skLineSegment(sketch, "E414", {"start": v(108.16, -81.48) * mm, "end": v(119.16, -81.48) * mm});
            skLineSegment(sketch, "E415", {"start": v(-18.64, -83) * mm, "end": v(-29.43, -83) * mm});
            skLineSegment(sketch, "E416", {"start": v(-18.43, -81.48) * mm, "end": v(-29.43, -81.48) * mm});
            skLineSegment(sketch, "E417", {"start": v(187.74, -130.36) * mm, "end": v(49.63, -130.36) * mm});
            skLineSegment(sketch, "E418", {"start": v(40.1, -130.36) * mm, "end": v(-105.22, -130.36) * mm});
            skLineSegment(sketch, "E419", {"start": v(187.74, -131.16) * mm, "end": v(49.63, -131.16) * mm});
            skLineSegment(sketch, "E420", {"start": v(40.1, -131.16) * mm, "end": v(-105.22, -131.16) * mm});
            skLineSegment(sketch, "E421", {"start": v(50.63, -132.01) * mm, "end": v(152.23, -132.01) * mm});
            skLineSegment(sketch, "E422", {"start": v(50.63, -134.28) * mm, "end": v(152.23, -134.28) * mm});
            skLineSegment(sketch, "E423", {"start": v(50.63, -134.85) * mm, "end": v(152.23, -134.85) * mm});
            skLineSegment(sketch, "E424", {"start": v(50.63, -132.01) * mm, "end": v(50.63, -134.85) * mm});
            skLineSegment(sketch, "E425", {"start": v(152.23, -132.01) * mm, "end": v(152.23, -134.85) * mm});
            skLineSegment(sketch, "E426", {"start": v(-62.42, -132.01) * mm, "end": v(39.18, -132.01) * mm});
            skLineSegment(sketch, "E427", {"start": v(-62.42, -134.28) * mm, "end": v(39.18, -134.28) * mm});
            skLineSegment(sketch, "E428", {"start": v(-62.42, -134.85) * mm, "end": v(39.18, -134.85) * mm});
            skLineSegment(sketch, "E429", {"start": v(-62.42, -132.01) * mm, "end": v(-62.42, -134.85) * mm});
            skLineSegment(sketch, "E430", {"start": v(39.18, -132.01) * mm, "end": v(39.18, -134.85) * mm});
            skLineSegment(sketch, "E431", {"start": v(22.26, -136.63) * mm, "end": v(22.26, -135.36) * mm});
            skLineSegment(sketch, "E432", {"start": v(9.05, -136.63) * mm, "end": v(9.05, -135.36) * mm});
            skLineSegment(sketch, "E433", {"start": v(20.85, -141.05) * mm, "end": v(20.85, -136.63) * mm});
            skLineSegment(sketch, "E434", {"start": v(10.46, -141.05) * mm, "end": v(10.46, -136.63) * mm});
            skLineSegment(sketch, "E435", {"start": v(18.1, -93.54) * mm, "end": v(18.1, -92.52) * mm});
            skLineSegment(sketch, "E436", {"start": v(18.1, -91.73) * mm, "end": v(18.1, -90.7) * mm});
            skLineSegment(sketch, "E437", {"start": v(18.1, -89.92) * mm, "end": v(18.1, -88.9) * mm});
            skLineSegment(sketch, "E438", {"start": v(18.1, -88.1) * mm, "end": v(18.1, -87.08) * mm});
            skLineSegment(sketch, "E439", {"start": v(18.1, -86.3) * mm, "end": v(18.1, -85.27) * mm});
            skLineSegment(sketch, "E440", {"start": v(18.1, -84.48) * mm, "end": v(18.1, -83.46) * mm});
            skLineSegment(sketch, "E441", {"start": v(18.1, -82.66) * mm, "end": v(18.1, -81.64) * mm});
            skLineSegment(sketch, "E442", {"start": v(18.1, -80.85) * mm, "end": v(18.1, -79.83) * mm});
            skLineSegment(sketch, "E443", {"start": v(18.1, -75.4) * mm, "end": v(18.1, -74.39) * mm});
            skLineSegment(sketch, "E444", {"start": v(13.22, -95.36) * mm, "end": v(13.22, -94.34) * mm});
            skLineSegment(sketch, "E445", {"start": v(13.22, -93.54) * mm, "end": v(13.22, -92.52) * mm});
            skLineSegment(sketch, "E446", {"start": v(13.22, -91.73) * mm, "end": v(13.22, -90.7) * mm});
            skLineSegment(sketch, "E447", {"start": v(13.22, -89.92) * mm, "end": v(13.22, -88.9) * mm});
            skLineSegment(sketch, "E448", {"start": v(13.22, -88.1) * mm, "end": v(13.22, -87.08) * mm});
            skLineSegment(sketch, "E449", {"start": v(13.22, -86.3) * mm, "end": v(13.22, -85.27) * mm});
            skLineSegment(sketch, "E450", {"start": v(13.22, -84.48) * mm, "end": v(13.22, -83.46) * mm});
            skLineSegment(sketch, "E451", {"start": v(13.22, -82.66) * mm, "end": v(13.22, -81.64) * mm});
            skLineSegment(sketch, "E452", {"start": v(13.22, -80.85) * mm, "end": v(13.22, -79.83) * mm});
            skLineSegment(sketch, "E453", {"start": v(12.53, -93.94) * mm, "end": v(13.22, -94.34) * mm});
            skLineSegment(sketch, "E454", {"start": v(12.53, -93.94) * mm, "end": v(13.22, -93.54) * mm});
            skLineSegment(sketch, "E455", {"start": v(12.53, -92.13) * mm, "end": v(13.22, -92.52) * mm});
            skLineSegment(sketch, "E456", {"start": v(12.53, -92.13) * mm, "end": v(13.22, -91.73) * mm});
            skLineSegment(sketch, "E457", {"start": v(18.78, -92.13) * mm, "end": v(18.1, -92.52) * mm});
            skLineSegment(sketch, "E458", {"start": v(18.78, -92.13) * mm, "end": v(18.1, -91.73) * mm});
            skLineSegment(sketch, "E459", {"start": v(18.78, -90.31) * mm, "end": v(18.1, -90.7) * mm});
            skLineSegment(sketch, "E460", {"start": v(18.78, -90.31) * mm, "end": v(18.1, -89.92) * mm});
            skLineSegment(sketch, "E461", {"start": v(12.53, -93.94) * mm, "end": v(18.78, -92.13) * mm});
            skLineSegment(sketch, "E462", {"start": v(12.53, -92.13) * mm, "end": v(18.78, -90.31) * mm});
            skLineSegment(sketch, "E463", {"start": v(13.22, -94.34) * mm, "end": v(18.1, -92.52) * mm});
            skLineSegment(sketch, "E464", {"start": v(13.22, -93.54) * mm, "end": v(18.1, -91.73) * mm});
            skLineSegment(sketch, "E465", {"start": v(13.22, -92.52) * mm, "end": v(18.1, -90.7) * mm});
            skLineSegment(sketch, "E466", {"start": v(13.22, -91.73) * mm, "end": v(18.1, -89.92) * mm});
            skLineSegment(sketch, "E467", {"start": v(12.53, -90.31) * mm, "end": v(13.22, -90.7) * mm});
            skLineSegment(sketch, "E468", {"start": v(12.53, -90.31) * mm, "end": v(13.22, -89.92) * mm});
            skLineSegment(sketch, "E469", {"start": v(12.53, -88.5) * mm, "end": v(13.22, -88.9) * mm});
            skLineSegment(sketch, "E470", {"start": v(12.53, -88.5) * mm, "end": v(13.22, -88.1) * mm});
            skLineSegment(sketch, "E471", {"start": v(18.78, -88.5) * mm, "end": v(18.1, -88.9) * mm});
            skLineSegment(sketch, "E472", {"start": v(18.78, -88.5) * mm, "end": v(18.1, -88.1) * mm});
            skLineSegment(sketch, "E473", {"start": v(18.78, -86.69) * mm, "end": v(18.1, -87.08) * mm});
            skLineSegment(sketch, "E474", {"start": v(18.78, -86.69) * mm, "end": v(18.1, -86.3) * mm});
            skLineSegment(sketch, "E475", {"start": v(12.53, -90.31) * mm, "end": v(18.78, -88.5) * mm});
            skLineSegment(sketch, "E476", {"start": v(12.53, -88.5) * mm, "end": v(18.78, -86.69) * mm});
            skLineSegment(sketch, "E477", {"start": v(13.22, -90.7) * mm, "end": v(18.1, -88.9) * mm});
            skLineSegment(sketch, "E478", {"start": v(13.22, -89.92) * mm, "end": v(18.1, -88.1) * mm});
            skLineSegment(sketch, "E479", {"start": v(13.22, -88.9) * mm, "end": v(18.1, -87.08) * mm});
            skLineSegment(sketch, "E480", {"start": v(13.22, -88.1) * mm, "end": v(18.1, -86.3) * mm});
            skLineSegment(sketch, "E481", {"start": v(12.53, -86.69) * mm, "end": v(13.22, -87.08) * mm});
            skLineSegment(sketch, "E482", {"start": v(12.53, -86.69) * mm, "end": v(13.22, -86.3) * mm});
            skLineSegment(sketch, "E483", {"start": v(18.78, -84.87) * mm, "end": v(18.1, -85.27) * mm});
            skLineSegment(sketch, "E484", {"start": v(18.78, -84.87) * mm, "end": v(18.1, -84.48) * mm});
            skLineSegment(sketch, "E485", {"start": v(12.53, -86.69) * mm, "end": v(18.78, -84.87) * mm});
            skLineSegment(sketch, "E486", {"start": v(13.22, -87.08) * mm, "end": v(18.1, -85.27) * mm});
            skLineSegment(sketch, "E487", {"start": v(13.22, -86.3) * mm, "end": v(18.1, -84.48) * mm});
            skLineSegment(sketch, "E488", {"start": v(12.53, -84.87) * mm, "end": v(13.22, -85.27) * mm});
            skLineSegment(sketch, "E489", {"start": v(12.53, -84.87) * mm, "end": v(13.22, -84.48) * mm});
            skLineSegment(sketch, "E490", {"start": v(12.53, -83.06) * mm, "end": v(13.22, -83.46) * mm});
            skLineSegment(sketch, "E491", {"start": v(12.53, -83.06) * mm, "end": v(13.22, -82.66) * mm});
            skLineSegment(sketch, "E492", {"start": v(18.78, -83.06) * mm, "end": v(18.1, -83.46) * mm});
            skLineSegment(sketch, "E493", {"start": v(18.78, -83.06) * mm, "end": v(18.1, -82.66) * mm});
            skLineSegment(sketch, "E494", {"start": v(18.78, -81.25) * mm, "end": v(18.1, -81.64) * mm});
            skLineSegment(sketch, "E495", {"start": v(18.78, -81.25) * mm, "end": v(18.1, -80.85) * mm});
            skLineSegment(sketch, "E496", {"start": v(12.53, -84.87) * mm, "end": v(18.78, -83.06) * mm});
            skLineSegment(sketch, "E497", {"start": v(12.53, -83.06) * mm, "end": v(18.78, -81.25) * mm});
            skLineSegment(sketch, "E498", {"start": v(13.22, -85.27) * mm, "end": v(18.1, -83.46) * mm});
            skLineSegment(sketch, "E499", {"start": v(13.22, -84.48) * mm, "end": v(18.1, -82.66) * mm});
            skLineSegment(sketch, "E500", {"start": v(13.22, -83.46) * mm, "end": v(18.1, -81.64) * mm});
            skLineSegment(sketch, "E501", {"start": v(13.22, -82.66) * mm, "end": v(18.1, -80.85) * mm});
            skLineSegment(sketch, "E502", {"start": v(12.53, -81.25) * mm, "end": v(13.22, -81.64) * mm});
            skLineSegment(sketch, "E503", {"start": v(12.53, -81.25) * mm, "end": v(13.22, -80.85) * mm});
            skLineSegment(sketch, "E504", {"start": v(13.22, -81.64) * mm, "end": v(18.1, -79.83) * mm});
            skLineSegment(sketch, "E505", {"start": v(12.53, -75.8) * mm, "end": v(13.22, -76.2) * mm});
            skLineSegment(sketch, "E506", {"start": v(12.53, -75.8) * mm, "end": v(13.22, -75.4) * mm});
            skLineSegment(sketch, "E507", {"start": v(18.78, -75.8) * mm, "end": v(18.1, -76.2) * mm});
            skLineSegment(sketch, "E508", {"start": v(18.78, -75.8) * mm, "end": v(18.1, -75.4) * mm});
            skLineSegment(sketch, "E509", {"start": v(18.78, -74) * mm, "end": v(18.1, -74.39) * mm});
            skLineSegment(sketch, "E510", {"start": v(18.78, -74) * mm, "end": v(18.1, -73.6) * mm});
            skLineSegment(sketch, "E511", {"start": v(9.05, -135.36) * mm, "end": v(22.26, -135.36) * mm});
            skLineSegment(sketch, "E512", {"start": v(9.05, -136.63) * mm, "end": v(22.26, -136.63) * mm});
            skLineSegment(sketch, "E513", {"start": v(11.15, -141.45) * mm, "end": v(20.15, -141.45) * mm});
            skLineSegment(sketch, "E514", {"start": v(13.06, -141.05) * mm, "end": v(13.06, -136.63) * mm});
            skLineSegment(sketch, "E515", {"start": v(18.25, -141.05) * mm, "end": v(18.25, -136.63) * mm});
            skLineSegment(sketch, "E516", {"start": v(11.15, -141.45) * mm, "end": v(10.46, -141.05) * mm});
            skLineSegment(sketch, "E517", {"start": v(20.15, -141.45) * mm, "end": v(20.85, -141.05) * mm});
            skLineSegment(sketch, "E518", {"start": v(17.55, -141.45) * mm, "end": v(18.25, -141.05) * mm});
            skLineSegment(sketch, "E519", {"start": v(12.36, -141.45) * mm, "end": v(13.06, -141.05) * mm});
            skLineSegment(sketch, "E520", {"start": v(18.95, -141.45) * mm, "end": v(18.25, -141.05) * mm});
            skLineSegment(sketch, "E521", {"start": v(13.75, -141.45) * mm, "end": v(13.06, -141.05) * mm});
            skLineSegment(sketch, "E522", {"start": v(13.22, -75.4) * mm, "end": v(13.22, -63.93) * mm});
            skLineSegment(sketch, "E523", {"start": v(17.44, -73.84) * mm, "end": v(17.44, -63.93) * mm});
            skLineSegment(sketch, "E524", {"start": v(15.33, -62.7) * mm, "end": v(13.22, -63.93) * mm});
            skLineSegment(sketch, "E525", {"start": v(15.33, -62.7) * mm, "end": v(17.44, -63.93) * mm});
            skLineSegment(sketch, "E526", {"start": v(15.33, -62.7) * mm, "end": v(15.33, -72.23) * mm});
            skLineSegment(sketch, "E527", {"start": v(12.53, -95.75) * mm, "end": v(13.22, -96.15) * mm});
            skLineSegment(sketch, "E528", {"start": v(12.53, -95.75) * mm, "end": v(13.22, -95.36) * mm});
            skLineSegment(sketch, "E529", {"start": v(18.78, -93.94) * mm, "end": v(18.1, -94.34) * mm});
            skLineSegment(sketch, "E530", {"start": v(18.78, -93.94) * mm, "end": v(18.1, -93.54) * mm});
            skLineSegment(sketch, "E531", {"start": v(12.53, -95.75) * mm, "end": v(18.78, -93.94) * mm});
            skLineSegment(sketch, "E532", {"start": v(13.22, -96.15) * mm, "end": v(18.1, -94.34) * mm});
            skLineSegment(sketch, "E533", {"start": v(13.22, -95.36) * mm, "end": v(18.1, -93.54) * mm});
            skLineSegment(sketch, "E534", {"start": v(13.22, -96.15) * mm, "end": v(13.22, -135.36) * mm});
            skLineSegment(sketch, "E535", {"start": v(18.1, -94.34) * mm, "end": v(18.1, -135.36) * mm});
            skLineSegment(sketch, "E536", {"start": v(-29.43, -83) * mm, "end": v(-29.43, -81.48) * mm});
            skLineSegment(sketch, "E537", {"start": v(119.16, -83) * mm, "end": v(119.16, -81.48) * mm});
            skLineSegment(sketch, "E538", {"start": v(119.2, -164.92) * mm, "end": v(119.6, -166.4) * mm});
            skLineSegment(sketch, "E539", {"start": v(-29.87, -166.4) * mm, "end": v(-29.47, -164.92) * mm});
            skLineSegment(sketch, "E540", {"start": v(-29.16, -165.55) * mm, "end": v(2.6, -165.55) * mm});
            skLineSegment(sketch, "E541", {"start": v(-29.16, -164.03) * mm, "end": v(2.6, -164.03) * mm});
            skLineSegment(sketch, "E542", {"start": v(-29.16, -164.03) * mm, "end": v(-29.16, -165.55) * mm});
            skLineSegment(sketch, "E543", {"start": v(2.6, -164.03) * mm, "end": v(2.6, -165.55) * mm});
            skLineSegment(sketch, "E544", {"start": v(87.33, -165.55) * mm, "end": v(119.08, -165.55) * mm});
            skLineSegment(sketch, "E545", {"start": v(87.33, -164.03) * mm, "end": v(119.08, -164.03) * mm});
            skLineSegment(sketch, "E546", {"start": v(87.33, -164.03) * mm, "end": v(87.33, -165.55) * mm});
            skLineSegment(sketch, "E547", {"start": v(119.08, -164.03) * mm, "end": v(119.08, -165.55) * mm});
            skLineSegment(sketch, "E548", {"start": v(-4.94, -85.56) * mm, "end": v(34.87, -85.56) * mm});
            skLineSegment(sketch, "E549", {"start": v(-4.94, -84.04) * mm, "end": v(34.87, -84.04) * mm});
            skLineSegment(sketch, "E550", {"start": v(-4.94, -84.04) * mm, "end": v(-4.94, -85.56) * mm});
            skLineSegment(sketch, "E551", {"start": v(34.87, -84.04) * mm, "end": v(34.87, -85.56) * mm});
            skLineSegment(sketch, "E552", {"start": v(55.88, -85.56) * mm, "end": v(94.6, -85.56) * mm});
            skLineSegment(sketch, "E553", {"start": v(55.88, -84.04) * mm, "end": v(94.6, -84.04) * mm});
            skLineSegment(sketch, "E554", {"start": v(55.88, -84.04) * mm, "end": v(55.88, -85.56) * mm});
            skLineSegment(sketch, "E555", {"start": v(94.6, -84.04) * mm, "end": v(94.6, -85.56) * mm});
            skLineSegment(sketch, "E556", {"start": v(-5.7, -170.24) * mm, "end": v(-17.48, -170.24) * mm});
            skLineSegment(sketch, "E557", {"start": v(-14.28, -168.36) * mm, "end": v(-8.9, -166.58) * mm});
            skLineSegment(sketch, "E558", {"start": v(-14.28, -168.36) * mm, "end": v(-13.6, -168.75) * mm});
            skLineSegment(sketch, "E559", {"start": v(-14.28, -168.36) * mm, "end": v(-13.6, -167.97) * mm});
            skLineSegment(sketch, "E560", {"start": v(-8.9, -166.58) * mm, "end": v(-9.58, -166.19) * mm});
            skLineSegment(sketch, "E561", {"start": v(-8.9, -166.58) * mm, "end": v(-9.58, -166.97) * mm});
            skLineSegment(sketch, "E562", {"start": v(-9.58, -166.19) * mm, "end": v(-13.6, -167.97) * mm});
            skLineSegment(sketch, "E563", {"start": v(-13.6, -168.75) * mm, "end": v(-9.58, -166.97) * mm});
            skLineSegment(sketch, "E564", {"start": v(-8.9, -164.8) * mm, "end": v(-9.58, -164.4) * mm});
            skLineSegment(sketch, "E565", {"start": v(-8.9, -164.8) * mm, "end": v(-9.58, -165.2) * mm});
            skLineSegment(sketch, "E566", {"start": v(-14.28, -166.58) * mm, "end": v(-8.9, -164.8) * mm});
            skLineSegment(sketch, "E567", {"start": v(-9.58, -164.4) * mm, "end": v(-13.6, -166.19) * mm});
            skLineSegment(sketch, "E568", {"start": v(-13.6, -166.97) * mm, "end": v(-9.58, -165.2) * mm});
            skLineSegment(sketch, "E569", {"start": v(-14.28, -166.58) * mm, "end": v(-13.6, -166.97) * mm});
            skLineSegment(sketch, "E570", {"start": v(-14.28, -166.58) * mm, "end": v(-13.6, -166.19) * mm});
            skLineSegment(sketch, "E571", {"start": v(-8.9, -163.02) * mm, "end": v(-9.58, -162.63) * mm});
            skLineSegment(sketch, "E572", {"start": v(-8.9, -163.02) * mm, "end": v(-9.58, -163.42) * mm});
            skLineSegment(sketch, "E573", {"start": v(-14.28, -164.8) * mm, "end": v(-8.9, -163.02) * mm});
            skLineSegment(sketch, "E574", {"start": v(-9.58, -162.63) * mm, "end": v(-13.6, -164.4) * mm});
            skLineSegment(sketch, "E575", {"start": v(-13.6, -165.2) * mm, "end": v(-9.58, -163.42) * mm});
            skLineSegment(sketch, "E576", {"start": v(-14.28, -164.8) * mm, "end": v(-13.6, -165.2) * mm});
            skLineSegment(sketch, "E577", {"start": v(-14.28, -164.8) * mm, "end": v(-13.6, -164.4) * mm});
            skLineSegment(sketch, "E578", {"start": v(-8.9, -161.24) * mm, "end": v(-9.58, -160.85) * mm});
            skLineSegment(sketch, "E579", {"start": v(-8.9, -161.24) * mm, "end": v(-9.58, -161.64) * mm});
            skLineSegment(sketch, "E580", {"start": v(-14.28, -163.02) * mm, "end": v(-8.9, -161.24) * mm});
            skLineSegment(sketch, "E581", {"start": v(-9.58, -160.85) * mm, "end": v(-13.6, -162.63) * mm});
            skLineSegment(sketch, "E582", {"start": v(-13.6, -163.42) * mm, "end": v(-9.58, -161.64) * mm});
            skLineSegment(sketch, "E583", {"start": v(-14.28, -163.02) * mm, "end": v(-13.6, -163.42) * mm});
            skLineSegment(sketch, "E584", {"start": v(-14.28, -163.02) * mm, "end": v(-13.6, -162.63) * mm});
            skLineSegment(sketch, "E585", {"start": v(-8.9, -159.46) * mm, "end": v(-9.58, -159.07) * mm});
            skLineSegment(sketch, "E586", {"start": v(-8.9, -159.46) * mm, "end": v(-9.58, -159.86) * mm});
            skLineSegment(sketch, "E587", {"start": v(-14.28, -161.24) * mm, "end": v(-8.9, -159.46) * mm});
            skLineSegment(sketch, "E588", {"start": v(-9.58, -159.07) * mm, "end": v(-13.6, -160.85) * mm});
            skLineSegment(sketch, "E589", {"start": v(-13.6, -161.64) * mm, "end": v(-9.58, -159.86) * mm});
            skLineSegment(sketch, "E590", {"start": v(-14.28, -161.24) * mm, "end": v(-13.6, -161.64) * mm});
            skLineSegment(sketch, "E591", {"start": v(-14.28, -161.24) * mm, "end": v(-13.6, -160.85) * mm});
            skLineSegment(sketch, "E592", {"start": v(-8.9, -157.68) * mm, "end": v(-9.58, -157.29) * mm});
            skLineSegment(sketch, "E593", {"start": v(-8.9, -157.68) * mm, "end": v(-9.58, -158.08) * mm});
            skLineSegment(sketch, "E594", {"start": v(-14.28, -159.46) * mm, "end": v(-8.9, -157.68) * mm});
            skLineSegment(sketch, "E595", {"start": v(-9.58, -157.29) * mm, "end": v(-13.6, -159.07) * mm});
            skLineSegment(sketch, "E596", {"start": v(-13.6, -159.86) * mm, "end": v(-9.58, -158.08) * mm});
            skLineSegment(sketch, "E597", {"start": v(-14.28, -159.46) * mm, "end": v(-13.6, -159.86) * mm});
            skLineSegment(sketch, "E598", {"start": v(-14.28, -159.46) * mm, "end": v(-13.6, -159.07) * mm});
            skLineSegment(sketch, "E599", {"start": v(-14.28, -157.68) * mm, "end": v(-11.6, -157.19) * mm});
            skLineSegment(sketch, "E600", {"start": v(-11.6, -157.19) * mm, "end": v(-13.6, -157.29) * mm});
            skLineSegment(sketch, "E601", {"start": v(-13.6, -158.08) * mm, "end": v(-11.6, -157.19) * mm});
            skLineSegment(sketch, "E602", {"start": v(-14.28, -157.68) * mm, "end": v(-13.6, -158.08) * mm});
            skLineSegment(sketch, "E603", {"start": v(-14.28, -157.68) * mm, "end": v(-13.6, -157.29) * mm});
            skLineSegment(sketch, "E604", {"start": v(-13.6, -158.08) * mm, "end": v(-13.6, -159.07) * mm});
            skLineSegment(sketch, "E605", {"start": v(-9.58, -158.08) * mm, "end": v(-9.58, -159.07) * mm});
            skLineSegment(sketch, "E606", {"start": v(-9.58, -159.86) * mm, "end": v(-9.58, -160.85) * mm});
            skLineSegment(sketch, "E607", {"start": v(-9.58, -161.64) * mm, "end": v(-9.58, -162.63) * mm});
            skLineSegment(sketch, "E608", {"start": v(-9.58, -163.42) * mm, "end": v(-9.58, -164.4) * mm});
            skLineSegment(sketch, "E609", {"start": v(-9.58, -165.2) * mm, "end": v(-9.58, -166.19) * mm});
            skLineSegment(sketch, "E610", {"start": v(-9.58, -166.97) * mm, "end": v(-9.58, -167.97) * mm});
            skLineSegment(sketch, "E611", {"start": v(-9.58, -168.75) * mm, "end": v(-9.58, -170.24) * mm});
            skLineSegment(sketch, "E612", {"start": v(-13.6, -168.75) * mm, "end": v(-13.6, -169.74) * mm});
            skLineSegment(sketch, "E613", {"start": v(-13.6, -166.97) * mm, "end": v(-13.6, -167.97) * mm});
            skLineSegment(sketch, "E614", {"start": v(-13.6, -165.2) * mm, "end": v(-13.6, -166.19) * mm});
            skLineSegment(sketch, "E615", {"start": v(-13.6, -163.42) * mm, "end": v(-13.6, -164.4) * mm});
            skLineSegment(sketch, "E616", {"start": v(-13.6, -161.64) * mm, "end": v(-13.6, -162.63) * mm});
            skLineSegment(sketch, "E617", {"start": v(-13.6, -159.86) * mm, "end": v(-13.6, -160.85) * mm});
            skLineSegment(sketch, "E618", {"start": v(-8.9, -168.36) * mm, "end": v(-9.58, -167.97) * mm});
            skLineSegment(sketch, "E619", {"start": v(-8.9, -168.36) * mm, "end": v(-9.58, -168.75) * mm});
            skLineSegment(sketch, "E620", {"start": v(-14.28, -170.14) * mm, "end": v(-8.9, -168.36) * mm});
            skLineSegment(sketch, "E621", {"start": v(-9.58, -167.97) * mm, "end": v(-13.6, -169.74) * mm});
            skLineSegment(sketch, "E622", {"start": v(-12.93, -170.24) * mm, "end": v(-9.58, -168.75) * mm});
            skLineSegment(sketch, "E623", {"start": v(-14.28, -170.14) * mm, "end": v(-13.6, -169.74) * mm});
            skLineSegment(sketch, "E624", {"start": v(-14.28, -170.14) * mm, "end": v(-14.11, -170.24) * mm});
            skLineSegment(sketch, "E625", {"start": v(-5.7, -171.12) * mm, "end": v(-17.48, -171.12) * mm});
            skLineSegment(sketch, "E626", {"start": v(-17.48, -170.24) * mm, "end": v(-17.48, -171.12) * mm});
            skLineSegment(sketch, "E627", {"start": v(-5.7, -170.24) * mm, "end": v(-5.7, -171.12) * mm});
            skLineSegment(sketch, "E628", {"start": v(-7.92, -174.54) * mm, "end": v(-15.33, -174.54) * mm});
            skLineSegment(sketch, "E629", {"start": v(-6.75, -171.12) * mm, "end": v(-6.75, -173.47) * mm});
            skLineSegment(sketch, "E630", {"start": v(-16.43, -171.12) * mm, "end": v(-16.43, -173.47) * mm});
            skLineSegment(sketch, "E631", {"start": v(-14.16, -173.47) * mm, "end": v(-14.16, -171.12) * mm});
            skLineSegment(sketch, "E632", {"start": v(-9.03, -173.47) * mm, "end": v(-9.03, -171.12) * mm});
            skArc(sketch, "E633", {"start": v(-14.16, -173.47) * mm, "mid": v(-11.6, -174.54) * mm, "end": v(-9.03, -173.47) * mm});
            skArc(sketch, "E634", {"start": v(-9.03, -173.47) * mm, "mid": v(-7.89, -174.54) * mm, "end": v(-6.75, -173.47) * mm});
            skArc(sketch, "E635", {"start": v(-16.43, -173.47) * mm, "mid": v(-15.3, -174.54) * mm, "end": v(-14.16, -173.47) * mm});
            skLineSegment(sketch, "E636", {"start": v(-13.6, -157.29) * mm, "end": v(-13.6, -152.35) * mm});
            skLineSegment(sketch, "E637", {"start": v(-9.58, -157.29) * mm, "end": v(-9.58, -152.35) * mm});
            skLineSegment(sketch, "E638", {"start": v(-11.6, -151.19) * mm, "end": v(-13.6, -152.35) * mm});
            skLineSegment(sketch, "E639", {"start": v(-11.6, -151.19) * mm, "end": v(-9.58, -152.35) * mm});
            skLineSegment(sketch, "E640", {"start": v(-11.6, -151.19) * mm, "end": v(-11.6, -153.73) * mm});
            skArc(sketch, "E641", {"start": v(-11.6, -153.73) * mm, "mid": v(-11, -155.15) * mm, "end": v(-9.58, -155.74) * mm});
            skLineSegment(sketch, "E642", {"start": v(107.15, -170.24) * mm, "end": v(95.36, -170.24) * mm});
            skLineSegment(sketch, "E643", {"start": v(98.56, -168.36) * mm, "end": v(103.94, -166.58) * mm});
            skLineSegment(sketch, "E644", {"start": v(98.56, -168.36) * mm, "end": v(99.24, -168.75) * mm});
            skLineSegment(sketch, "E645", {"start": v(98.56, -168.36) * mm, "end": v(99.24, -167.97) * mm});
            skLineSegment(sketch, "E646", {"start": v(103.94, -166.58) * mm, "end": v(103.26, -166.19) * mm});
            skLineSegment(sketch, "E647", {"start": v(103.94, -166.58) * mm, "end": v(103.26, -166.97) * mm});
            skLineSegment(sketch, "E648", {"start": v(103.26, -166.19) * mm, "end": v(99.24, -167.97) * mm});
            skLineSegment(sketch, "E649", {"start": v(99.24, -168.75) * mm, "end": v(103.26, -166.97) * mm});
            skLineSegment(sketch, "E650", {"start": v(103.94, -164.8) * mm, "end": v(103.26, -164.4) * mm});
            skLineSegment(sketch, "E651", {"start": v(103.94, -164.8) * mm, "end": v(103.26, -165.2) * mm});
            skLineSegment(sketch, "E652", {"start": v(98.56, -166.58) * mm, "end": v(103.94, -164.8) * mm});
            skLineSegment(sketch, "E653", {"start": v(103.26, -164.4) * mm, "end": v(99.24, -166.19) * mm});
            skLineSegment(sketch, "E654", {"start": v(99.24, -166.97) * mm, "end": v(103.26, -165.2) * mm});
            skLineSegment(sketch, "E655", {"start": v(98.56, -166.58) * mm, "end": v(99.24, -166.97) * mm});
            skLineSegment(sketch, "E656", {"start": v(98.56, -166.58) * mm, "end": v(99.24, -166.19) * mm});
            skLineSegment(sketch, "E657", {"start": v(103.94, -163.02) * mm, "end": v(103.26, -162.63) * mm});
            skLineSegment(sketch, "E658", {"start": v(103.94, -163.02) * mm, "end": v(103.26, -163.42) * mm});
            skLineSegment(sketch, "E659", {"start": v(98.56, -164.8) * mm, "end": v(103.94, -163.02) * mm});
            skLineSegment(sketch, "E660", {"start": v(103.26, -162.63) * mm, "end": v(99.24, -164.4) * mm});
            skLineSegment(sketch, "E661", {"start": v(99.24, -165.2) * mm, "end": v(103.26, -163.42) * mm});
            skLineSegment(sketch, "E662", {"start": v(98.56, -164.8) * mm, "end": v(99.24, -165.2) * mm});
            skLineSegment(sketch, "E663", {"start": v(98.56, -164.8) * mm, "end": v(99.24, -164.4) * mm});
            skLineSegment(sketch, "E664", {"start": v(103.94, -161.24) * mm, "end": v(103.26, -160.85) * mm});
            skLineSegment(sketch, "E665", {"start": v(103.94, -161.24) * mm, "end": v(103.26, -161.64) * mm});
            skLineSegment(sketch, "E666", {"start": v(98.56, -163.02) * mm, "end": v(103.94, -161.24) * mm});
            skLineSegment(sketch, "E667", {"start": v(103.26, -160.85) * mm, "end": v(99.24, -162.63) * mm});
            skLineSegment(sketch, "E668", {"start": v(99.24, -163.42) * mm, "end": v(103.26, -161.64) * mm});
            skLineSegment(sketch, "E669", {"start": v(98.56, -163.02) * mm, "end": v(99.24, -163.42) * mm});
            skLineSegment(sketch, "E670", {"start": v(98.56, -163.02) * mm, "end": v(99.24, -162.63) * mm});
            skLineSegment(sketch, "E671", {"start": v(103.94, -159.46) * mm, "end": v(103.26, -159.07) * mm});
            skLineSegment(sketch, "E672", {"start": v(103.94, -159.46) * mm, "end": v(103.26, -159.86) * mm});
            skLineSegment(sketch, "E673", {"start": v(98.56, -161.24) * mm, "end": v(103.94, -159.46) * mm});
            skLineSegment(sketch, "E674", {"start": v(103.26, -159.07) * mm, "end": v(99.24, -160.85) * mm});
            skLineSegment(sketch, "E675", {"start": v(99.24, -161.64) * mm, "end": v(103.26, -159.86) * mm});
            skLineSegment(sketch, "E676", {"start": v(98.56, -161.24) * mm, "end": v(99.24, -161.64) * mm});
            skLineSegment(sketch, "E677", {"start": v(98.56, -161.24) * mm, "end": v(99.24, -160.85) * mm});
            skLineSegment(sketch, "E678", {"start": v(103.94, -157.68) * mm, "end": v(103.26, -157.29) * mm});
            skLineSegment(sketch, "E679", {"start": v(103.94, -157.68) * mm, "end": v(103.26, -158.08) * mm});
            skLineSegment(sketch, "E680", {"start": v(98.56, -159.46) * mm, "end": v(103.94, -157.68) * mm});
            skLineSegment(sketch, "E681", {"start": v(103.26, -157.29) * mm, "end": v(99.24, -159.07) * mm});
            skLineSegment(sketch, "E682", {"start": v(99.24, -159.86) * mm, "end": v(103.26, -158.08) * mm});
            skLineSegment(sketch, "E683", {"start": v(98.56, -159.46) * mm, "end": v(99.24, -159.86) * mm});
            skLineSegment(sketch, "E684", {"start": v(98.56, -159.46) * mm, "end": v(99.24, -159.07) * mm});
            skLineSegment(sketch, "E685", {"start": v(98.56, -157.68) * mm, "end": v(101.25, -157.19) * mm});
            skLineSegment(sketch, "E686", {"start": v(101.25, -157.19) * mm, "end": v(99.24, -157.29) * mm});
            skLineSegment(sketch, "E687", {"start": v(99.24, -158.08) * mm, "end": v(101.25, -157.19) * mm});
            skLineSegment(sketch, "E688", {"start": v(98.56, -157.68) * mm, "end": v(99.24, -158.08) * mm});
            skLineSegment(sketch, "E689", {"start": v(98.56, -157.68) * mm, "end": v(99.24, -157.29) * mm});
            skLineSegment(sketch, "E690", {"start": v(99.24, -158.08) * mm, "end": v(99.24, -159.07) * mm});
            skLineSegment(sketch, "E691", {"start": v(103.26, -158.08) * mm, "end": v(103.26, -159.07) * mm});
            skLineSegment(sketch, "E692", {"start": v(103.26, -159.86) * mm, "end": v(103.26, -160.85) * mm});
            skLineSegment(sketch, "E693", {"start": v(103.26, -161.64) * mm, "end": v(103.26, -162.63) * mm});
            skLineSegment(sketch, "E694", {"start": v(103.26, -163.42) * mm, "end": v(103.26, -164.4) * mm});
            skLineSegment(sketch, "E695", {"start": v(103.26, -165.2) * mm, "end": v(103.26, -166.19) * mm});
            skLineSegment(sketch, "E696", {"start": v(103.26, -166.97) * mm, "end": v(103.26, -167.97) * mm});
            skLineSegment(sketch, "E697", {"start": v(103.26, -168.75) * mm, "end": v(103.26, -170.24) * mm});
            skLineSegment(sketch, "E698", {"start": v(99.24, -168.75) * mm, "end": v(99.24, -169.74) * mm});
            skLineSegment(sketch, "E699", {"start": v(99.24, -166.97) * mm, "end": v(99.24, -167.97) * mm});
            skLineSegment(sketch, "E700", {"start": v(99.24, -165.2) * mm, "end": v(99.24, -166.19) * mm});
            skLineSegment(sketch, "E701", {"start": v(99.24, -163.42) * mm, "end": v(99.24, -164.4) * mm});
            skLineSegment(sketch, "E702", {"start": v(99.24, -161.64) * mm, "end": v(99.24, -162.63) * mm});
            skLineSegment(sketch, "E703", {"start": v(99.24, -159.86) * mm, "end": v(99.24, -160.85) * mm});
            skLineSegment(sketch, "E704", {"start": v(103.94, -168.36) * mm, "end": v(103.26, -167.97) * mm});
            skLineSegment(sketch, "E705", {"start": v(103.94, -168.36) * mm, "end": v(103.26, -168.75) * mm});
            skLineSegment(sketch, "E706", {"start": v(98.56, -170.14) * mm, "end": v(103.94, -168.36) * mm});
            skLineSegment(sketch, "E707", {"start": v(103.26, -167.97) * mm, "end": v(99.24, -169.74) * mm});
            skLineSegment(sketch, "E708", {"start": v(99.91, -170.24) * mm, "end": v(103.26, -168.75) * mm});
            skLineSegment(sketch, "E709", {"start": v(98.56, -170.14) * mm, "end": v(99.24, -169.74) * mm});
            skLineSegment(sketch, "E710", {"start": v(98.56, -170.14) * mm, "end": v(98.73, -170.24) * mm});
            skLineSegment(sketch, "E711", {"start": v(107.15, -171.12) * mm, "end": v(95.36, -171.12) * mm});
            skLineSegment(sketch, "E712", {"start": v(95.36, -170.24) * mm, "end": v(95.36, -171.12) * mm});
            skLineSegment(sketch, "E713", {"start": v(107.15, -170.24) * mm, "end": v(107.15, -171.12) * mm});
            skLineSegment(sketch, "E714", {"start": v(104.92, -174.54) * mm, "end": v(97.51, -174.54) * mm});
            skLineSegment(sketch, "E715", {"start": v(106.1, -171.12) * mm, "end": v(106.1, -173.47) * mm});
            skLineSegment(sketch, "E716", {"start": v(96.41, -171.12) * mm, "end": v(96.41, -173.47) * mm});
            skLineSegment(sketch, "E717", {"start": v(98.69, -173.47) * mm, "end": v(98.69, -171.12) * mm});
            skLineSegment(sketch, "E718", {"start": v(103.82, -173.47) * mm, "end": v(103.82, -171.12) * mm});
            skArc(sketch, "E719", {"start": v(98.69, -173.47) * mm, "mid": v(101.25, -174.54) * mm, "end": v(103.82, -173.47) * mm});
            skArc(sketch, "E720", {"start": v(103.82, -173.47) * mm, "mid": v(104.95, -174.54) * mm, "end": v(106.1, -173.47) * mm});
            skArc(sketch, "E721", {"start": v(96.41, -173.47) * mm, "mid": v(97.55, -174.54) * mm, "end": v(98.69, -173.47) * mm});
            skLineSegment(sketch, "E722", {"start": v(99.24, -157.29) * mm, "end": v(99.24, -152.35) * mm});
            skLineSegment(sketch, "E723", {"start": v(103.26, -157.29) * mm, "end": v(103.26, -152.35) * mm});
            skLineSegment(sketch, "E724", {"start": v(101.25, -151.19) * mm, "end": v(99.24, -152.35) * mm});
            skLineSegment(sketch, "E725", {"start": v(101.25, -151.19) * mm, "end": v(103.26, -152.35) * mm});
            skLineSegment(sketch, "E726", {"start": v(101.25, -151.19) * mm, "end": v(101.25, -153.73) * mm});
            skArc(sketch, "E727", {"start": v(101.25, -153.73) * mm, "mid": v(101.84, -155.15) * mm, "end": v(103.26, -155.74) * mm});
            skLineSegment(sketch, "E728", {"start": v(-9.09, 41.6) * mm, "end": v(-12.13, 41.6) * mm});
            skLineSegment(sketch, "E729", {"start": v(-12.13, 41.6) * mm, "end": v(-12.13, 56.84) * mm});
            skLineSegment(sketch, "E730", {"start": v(-9.09, 41.6) * mm, "end": v(-9.09, 56.84) * mm});
            skArc(sketch, "E731", {"start": v(-8.32, 57.6) * mm, "mid": v(-8.86, 57.38) * mm, "end": v(-9.09, 56.84) * mm});
            skArc(sketch, "E732", {"start": v(-8.32, 60.65) * mm, "mid": v(-11.02, 59.53) * mm, "end": v(-12.13, 56.84) * mm});
            skLineSegment(sketch, "E733", {"start": v(-8.32, 60.65) * mm, "end": v(40.73, 60.65) * mm});
            skLineSegment(sketch, "E734", {"start": v(-8.32, 57.6) * mm, "end": v(40.73, 57.6) * mm});
            skArc(sketch, "E735", {"start": v(41.5, 56.84) * mm, "mid": v(41.27, 57.38) * mm, "end": v(40.73, 57.6) * mm});
            skArc(sketch, "E736", {"start": v(44.54, 56.84) * mm, "mid": v(43.43, 59.53) * mm, "end": v(40.73, 60.65) * mm});
            skLineSegment(sketch, "E737", {"start": v(44.54, 56.84) * mm, "end": v(44.54, -75.94) * mm});
            skLineSegment(sketch, "E738", {"start": v(41.5, 56.84) * mm, "end": v(41.5, -75.94) * mm});
            skLineSegment(sketch, "E739", {"start": v(98.81, 41.6) * mm, "end": v(101.86, 41.6) * mm});
            skLineSegment(sketch, "E740", {"start": v(101.86, 41.6) * mm, "end": v(101.86, 56.84) * mm});
            skLineSegment(sketch, "E741", {"start": v(98.81, 41.6) * mm, "end": v(98.81, 56.84) * mm});
            skArc(sketch, "E742", {"start": v(98.81, 56.84) * mm, "mid": v(98.59, 57.38) * mm, "end": v(98.05, 57.6) * mm});
            skArc(sketch, "E743", {"start": v(101.86, 56.84) * mm, "mid": v(100.74, 59.53) * mm, "end": v(98.05, 60.65) * mm});
            skLineSegment(sketch, "E744", {"start": v(98.05, 60.65) * mm, "end": v(49, 60.65) * mm});
            skLineSegment(sketch, "E745", {"start": v(98.05, 57.6) * mm, "end": v(49, 57.6) * mm});
            skArc(sketch, "E746", {"start": v(49, 57.6) * mm, "mid": v(48.45, 57.38) * mm, "end": v(48.23, 56.84) * mm});
            skArc(sketch, "E747", {"start": v(49, 60.65) * mm, "mid": v(46.3, 59.53) * mm, "end": v(45.18, 56.84) * mm});
            skLineSegment(sketch, "E748", {"start": v(45.18, 56.84) * mm, "end": v(45.18, -75.94) * mm});
            skLineSegment(sketch, "E749", {"start": v(48.23, 56.84) * mm, "end": v(48.23, -75.94) * mm});
            skLineSegment(sketch, "E750", {"start": v(83.37, -136.63) * mm, "end": v(83.37, -135.36) * mm});
            skLineSegment(sketch, "E751", {"start": v(70.16, -136.63) * mm, "end": v(70.16, -135.36) * mm});
            skLineSegment(sketch, "E752", {"start": v(81.96, -141.05) * mm, "end": v(81.96, -136.63) * mm});
            skLineSegment(sketch, "E753", {"start": v(71.57, -141.05) * mm, "end": v(71.57, -136.63) * mm});
            skLineSegment(sketch, "E754", {"start": v(79.2, -93.54) * mm, "end": v(79.2, -92.52) * mm});
            skLineSegment(sketch, "E755", {"start": v(79.2, -91.73) * mm, "end": v(79.2, -90.7) * mm});
            skLineSegment(sketch, "E756", {"start": v(79.2, -89.92) * mm, "end": v(79.2, -88.9) * mm});
            skLineSegment(sketch, "E757", {"start": v(79.2, -88.1) * mm, "end": v(79.2, -87.08) * mm});
            skLineSegment(sketch, "E758", {"start": v(79.2, -86.3) * mm, "end": v(79.2, -85.27) * mm});
            skLineSegment(sketch, "E759", {"start": v(79.2, -84.48) * mm, "end": v(79.2, -83.46) * mm});
            skLineSegment(sketch, "E760", {"start": v(79.2, -82.66) * mm, "end": v(79.2, -81.64) * mm});
            skLineSegment(sketch, "E761", {"start": v(79.2, -80.85) * mm, "end": v(79.2, -79.83) * mm});
            skLineSegment(sketch, "E762", {"start": v(79.2, -79.04) * mm, "end": v(79.2, -78.01) * mm});
            skLineSegment(sketch, "E763", {"start": v(79.2, -77.22) * mm, "end": v(79.2, -76.2) * mm});
            skLineSegment(sketch, "E764", {"start": v(79.2, -75.4) * mm, "end": v(79.2, -74.39) * mm});
            skLineSegment(sketch, "E765", {"start": v(74.32, -95.36) * mm, "end": v(74.32, -94.34) * mm});
            skLineSegment(sketch, "E766", {"start": v(74.32, -93.54) * mm, "end": v(74.32, -92.52) * mm});
            skLineSegment(sketch, "E767", {"start": v(74.32, -91.73) * mm, "end": v(74.32, -90.7) * mm});
            skLineSegment(sketch, "E768", {"start": v(74.32, -89.92) * mm, "end": v(74.32, -88.9) * mm});
            skLineSegment(sketch, "E769", {"start": v(74.32, -88.1) * mm, "end": v(74.32, -87.08) * mm});
            skLineSegment(sketch, "E770", {"start": v(74.32, -86.3) * mm, "end": v(74.32, -85.27) * mm});
            skLineSegment(sketch, "E771", {"start": v(74.32, -84.48) * mm, "end": v(74.32, -83.46) * mm});
            skLineSegment(sketch, "E772", {"start": v(74.32, -82.66) * mm, "end": v(74.32, -81.64) * mm});
            skLineSegment(sketch, "E773", {"start": v(74.32, -80.85) * mm, "end": v(74.32, -79.83) * mm});
            skLineSegment(sketch, "E774", {"start": v(74.32, -79.04) * mm, "end": v(74.32, -78.01) * mm});
            skLineSegment(sketch, "E775", {"start": v(74.32, -77.22) * mm, "end": v(74.32, -76.2) * mm});
            skLineSegment(sketch, "E776", {"start": v(73.64, -93.94) * mm, "end": v(74.32, -94.34) * mm});
            skLineSegment(sketch, "E777", {"start": v(73.64, -93.94) * mm, "end": v(74.32, -93.54) * mm});
            skLineSegment(sketch, "E778", {"start": v(73.64, -92.13) * mm, "end": v(74.32, -92.52) * mm});
            skLineSegment(sketch, "E779", {"start": v(73.64, -92.13) * mm, "end": v(74.32, -91.73) * mm});
            skLineSegment(sketch, "E780", {"start": v(79.89, -92.13) * mm, "end": v(79.2, -92.52) * mm});
            skLineSegment(sketch, "E781", {"start": v(79.89, -92.13) * mm, "end": v(79.2, -91.73) * mm});
            skLineSegment(sketch, "E782", {"start": v(79.89, -90.31) * mm, "end": v(79.2, -90.7) * mm});
            skLineSegment(sketch, "E783", {"start": v(79.89, -90.31) * mm, "end": v(79.2, -89.92) * mm});
            skLineSegment(sketch, "E784", {"start": v(73.64, -93.94) * mm, "end": v(79.89, -92.13) * mm});
            skLineSegment(sketch, "E785", {"start": v(73.64, -92.13) * mm, "end": v(79.89, -90.31) * mm});
            skLineSegment(sketch, "E786", {"start": v(74.32, -94.34) * mm, "end": v(79.2, -92.52) * mm});
            skLineSegment(sketch, "E787", {"start": v(74.32, -93.54) * mm, "end": v(79.2, -91.73) * mm});
            skLineSegment(sketch, "E788", {"start": v(74.32, -92.52) * mm, "end": v(79.2, -90.7) * mm});
            skLineSegment(sketch, "E789", {"start": v(74.32, -91.73) * mm, "end": v(79.2, -89.92) * mm});
            skLineSegment(sketch, "E790", {"start": v(73.64, -90.31) * mm, "end": v(74.32, -90.7) * mm});
            skLineSegment(sketch, "E791", {"start": v(73.64, -90.31) * mm, "end": v(74.32, -89.92) * mm});
            skLineSegment(sketch, "E792", {"start": v(73.64, -88.5) * mm, "end": v(74.32, -88.9) * mm});
            skLineSegment(sketch, "E793", {"start": v(73.64, -88.5) * mm, "end": v(74.32, -88.1) * mm});
            skLineSegment(sketch, "E794", {"start": v(79.89, -88.5) * mm, "end": v(79.2, -88.9) * mm});
            skLineSegment(sketch, "E795", {"start": v(79.89, -88.5) * mm, "end": v(79.2, -88.1) * mm});
            skLineSegment(sketch, "E796", {"start": v(79.89, -86.69) * mm, "end": v(79.2, -87.08) * mm});
            skLineSegment(sketch, "E797", {"start": v(79.89, -86.69) * mm, "end": v(79.2, -86.3) * mm});
            skLineSegment(sketch, "E798", {"start": v(73.64, -90.31) * mm, "end": v(79.89, -88.5) * mm});
            skLineSegment(sketch, "E799", {"start": v(73.64, -88.5) * mm, "end": v(79.89, -86.69) * mm});
            skLineSegment(sketch, "E800", {"start": v(74.32, -90.7) * mm, "end": v(79.2, -88.9) * mm});
            skLineSegment(sketch, "E801", {"start": v(74.32, -89.92) * mm, "end": v(79.2, -88.1) * mm});
            skLineSegment(sketch, "E802", {"start": v(74.32, -88.9) * mm, "end": v(79.2, -87.08) * mm});
            skLineSegment(sketch, "E803", {"start": v(74.32, -88.1) * mm, "end": v(79.2, -86.3) * mm});
            skLineSegment(sketch, "E804", {"start": v(73.64, -86.69) * mm, "end": v(74.32, -87.08) * mm});
            skLineSegment(sketch, "E805", {"start": v(73.64, -86.69) * mm, "end": v(74.32, -86.3) * mm});
            skLineSegment(sketch, "E806", {"start": v(79.89, -84.87) * mm, "end": v(79.2, -85.27) * mm});
            skLineSegment(sketch, "E807", {"start": v(79.89, -84.87) * mm, "end": v(79.2, -84.48) * mm});
            skLineSegment(sketch, "E808", {"start": v(73.64, -86.69) * mm, "end": v(79.89, -84.87) * mm});
            skLineSegment(sketch, "E809", {"start": v(74.32, -87.08) * mm, "end": v(79.2, -85.27) * mm});
            skLineSegment(sketch, "E810", {"start": v(74.32, -86.3) * mm, "end": v(79.2, -84.48) * mm});
            skLineSegment(sketch, "E811", {"start": v(73.64, -84.87) * mm, "end": v(74.32, -85.27) * mm});
            skLineSegment(sketch, "E812", {"start": v(73.64, -84.87) * mm, "end": v(74.32, -84.48) * mm});
            skLineSegment(sketch, "E813", {"start": v(73.64, -83.06) * mm, "end": v(74.32, -83.46) * mm});
            skLineSegment(sketch, "E814", {"start": v(73.64, -83.06) * mm, "end": v(74.32, -82.66) * mm});
            skLineSegment(sketch, "E815", {"start": v(79.89, -83.06) * mm, "end": v(79.2, -83.46) * mm});
            skLineSegment(sketch, "E816", {"start": v(79.89, -83.06) * mm, "end": v(79.2, -82.66) * mm});
            skLineSegment(sketch, "E817", {"start": v(79.89, -81.25) * mm, "end": v(79.2, -81.64) * mm});
            skLineSegment(sketch, "E818", {"start": v(79.89, -81.25) * mm, "end": v(79.2, -80.85) * mm});
            skLineSegment(sketch, "E819", {"start": v(73.64, -84.87) * mm, "end": v(79.89, -83.06) * mm});
            skLineSegment(sketch, "E820", {"start": v(73.64, -83.06) * mm, "end": v(79.89, -81.25) * mm});
            skLineSegment(sketch, "E821", {"start": v(74.32, -85.27) * mm, "end": v(79.2, -83.46) * mm});
            skLineSegment(sketch, "E822", {"start": v(74.32, -84.48) * mm, "end": v(79.2, -82.66) * mm});
            skLineSegment(sketch, "E823", {"start": v(74.32, -83.46) * mm, "end": v(79.2, -81.64) * mm});
            skLineSegment(sketch, "E824", {"start": v(74.32, -82.66) * mm, "end": v(79.2, -80.85) * mm});
            skLineSegment(sketch, "E825", {"start": v(73.64, -81.25) * mm, "end": v(74.32, -81.64) * mm});
            skLineSegment(sketch, "E826", {"start": v(73.64, -81.25) * mm, "end": v(74.32, -80.85) * mm});
            skLineSegment(sketch, "E827", {"start": v(73.64, -79.43) * mm, "end": v(74.32, -79.83) * mm});
            skLineSegment(sketch, "E828", {"start": v(73.64, -79.43) * mm, "end": v(74.32, -79.04) * mm});
            skLineSegment(sketch, "E829", {"start": v(79.89, -79.43) * mm, "end": v(79.2, -79.83) * mm});
            skLineSegment(sketch, "E830", {"start": v(79.89, -79.43) * mm, "end": v(79.2, -79.04) * mm});
            skLineSegment(sketch, "E831", {"start": v(79.89, -77.62) * mm, "end": v(79.2, -78.01) * mm});
            skLineSegment(sketch, "E832", {"start": v(79.89, -77.62) * mm, "end": v(79.2, -77.22) * mm});
            skLineSegment(sketch, "E833", {"start": v(73.64, -81.25) * mm, "end": v(79.89, -79.43) * mm});
            skLineSegment(sketch, "E834", {"start": v(73.64, -79.43) * mm, "end": v(79.89, -77.62) * mm});
            skLineSegment(sketch, "E835", {"start": v(74.32, -81.64) * mm, "end": v(79.2, -79.83) * mm});
            skLineSegment(sketch, "E836", {"start": v(74.32, -80.85) * mm, "end": v(79.2, -79.04) * mm});
            skLineSegment(sketch, "E837", {"start": v(74.32, -79.83) * mm, "end": v(79.2, -78.01) * mm});
            skLineSegment(sketch, "E838", {"start": v(74.32, -79.04) * mm, "end": v(79.2, -77.22) * mm});
            skLineSegment(sketch, "E839", {"start": v(73.64, -77.62) * mm, "end": v(74.32, -78.01) * mm});
            skLineSegment(sketch, "E840", {"start": v(73.64, -77.62) * mm, "end": v(74.32, -77.22) * mm});
            skLineSegment(sketch, "E841", {"start": v(73.64, -75.8) * mm, "end": v(74.32, -76.2) * mm});
            skLineSegment(sketch, "E842", {"start": v(73.64, -75.8) * mm, "end": v(74.32, -75.4) * mm});
            skLineSegment(sketch, "E843", {"start": v(79.89, -75.8) * mm, "end": v(79.2, -76.2) * mm});
            skLineSegment(sketch, "E844", {"start": v(79.89, -75.8) * mm, "end": v(79.2, -75.4) * mm});
            skLineSegment(sketch, "E845", {"start": v(79.89, -74) * mm, "end": v(79.2, -74.39) * mm});
            skLineSegment(sketch, "E846", {"start": v(79.89, -74) * mm, "end": v(79.2, -73.6) * mm});
            skLineSegment(sketch, "E847", {"start": v(73.64, -77.62) * mm, "end": v(79.89, -75.8) * mm});
            skLineSegment(sketch, "E848", {"start": v(73.64, -75.8) * mm, "end": v(79.89, -74) * mm});
            skLineSegment(sketch, "E849", {"start": v(74.32, -78.01) * mm, "end": v(79.2, -76.2) * mm});
            skLineSegment(sketch, "E850", {"start": v(74.32, -77.22) * mm, "end": v(79.2, -75.4) * mm});
            skLineSegment(sketch, "E851", {"start": v(74.32, -76.2) * mm, "end": v(79.2, -74.39) * mm});
            skLineSegment(sketch, "E852", {"start": v(74.32, -75.4) * mm, "end": v(79.2, -73.6) * mm});
            skLineSegment(sketch, "E853", {"start": v(70.16, -135.36) * mm, "end": v(83.37, -135.36) * mm});
            skLineSegment(sketch, "E854", {"start": v(70.16, -136.63) * mm, "end": v(83.37, -136.63) * mm});
            skLineSegment(sketch, "E855", {"start": v(72.26, -141.45) * mm, "end": v(81.26, -141.45) * mm});
            skLineSegment(sketch, "E856", {"start": v(74.16, -141.05) * mm, "end": v(74.16, -136.63) * mm});
            skLineSegment(sketch, "E857", {"start": v(79.36, -141.05) * mm, "end": v(79.36, -136.63) * mm});
            skLineSegment(sketch, "E858", {"start": v(72.26, -141.45) * mm, "end": v(71.57, -141.05) * mm});
            skLineSegment(sketch, "E859", {"start": v(81.26, -141.45) * mm, "end": v(81.96, -141.05) * mm});
            skLineSegment(sketch, "E860", {"start": v(78.66, -141.45) * mm, "end": v(79.36, -141.05) * mm});
            skLineSegment(sketch, "E861", {"start": v(73.47, -141.45) * mm, "end": v(74.16, -141.05) * mm});
            skLineSegment(sketch, "E862", {"start": v(80.05, -141.45) * mm, "end": v(79.36, -141.05) * mm});
            skLineSegment(sketch, "E863", {"start": v(74.86, -141.45) * mm, "end": v(74.16, -141.05) * mm});
            skLineSegment(sketch, "E864", {"start": v(74.32, -75.4) * mm, "end": v(74.32, -63.93) * mm});
            skLineSegment(sketch, "E865", {"start": v(78.55, -73.84) * mm, "end": v(78.55, -63.93) * mm});
            skLineSegment(sketch, "E866", {"start": v(76.44, -62.7) * mm, "end": v(74.32, -63.93) * mm});
            skLineSegment(sketch, "E867", {"start": v(76.44, -62.7) * mm, "end": v(78.55, -63.93) * mm});
            skLineSegment(sketch, "E868", {"start": v(76.44, -62.7) * mm, "end": v(76.44, -72.23) * mm});
            skArc(sketch, "E869", {"start": v(76.44, -72.23) * mm, "mid": v(76.77, -73.38) * mm, "end": v(77.68, -74.16) * mm});
            skLineSegment(sketch, "E870", {"start": v(73.64, -95.75) * mm, "end": v(74.32, -96.15) * mm});
            skLineSegment(sketch, "E871", {"start": v(73.64, -95.75) * mm, "end": v(74.32, -95.36) * mm});
            skLineSegment(sketch, "E872", {"start": v(79.89, -93.94) * mm, "end": v(79.2, -94.34) * mm});
            skLineSegment(sketch, "E873", {"start": v(79.89, -93.94) * mm, "end": v(79.2, -93.54) * mm});
            skLineSegment(sketch, "E874", {"start": v(73.64, -95.75) * mm, "end": v(79.89, -93.94) * mm});
            skLineSegment(sketch, "E875", {"start": v(74.32, -96.15) * mm, "end": v(79.2, -94.34) * mm});
            skLineSegment(sketch, "E876", {"start": v(74.32, -95.36) * mm, "end": v(79.2, -93.54) * mm});
            skLineSegment(sketch, "E877", {"start": v(74.32, -96.15) * mm, "end": v(74.32, -135.36) * mm});
            skLineSegment(sketch, "E878", {"start": v(79.2, -94.34) * mm, "end": v(79.2, -135.36) * mm});
            skSolve(sketch);
        }
        {
            var Q0;
            Q0=makeQuery(id+"F0.imprint","IMPRINT",FACE,{"disambiguationData":[TD([[makeQuery(id+"F0.imprint","IMPRINT",EDGE,{"derivedFrom":sQuery(id+"F0.wireOp",EDGE,"E376")}),1.0]])]});
            extrude(context, id + "F1", {"entities" : qUnion([Q0]), "depth" : 2438.4 * mm});
        }
        {
            var Q0;
            Q0=makeQuery(id+"F1.opExtrude","SWEPT_FACE",FACE,{"disambiguationData":[OSD([sQuery(id+"F0.wireOp",EDGE,"E733")])]});
            var sketch = newSketch(context, id + "F2", { "sketchPlane" : qUnion([Q0])});
            skLineSegment(sketch, "E879", {"start": v(-8.32, 0) * mm, "end": v(40.73, 0) * mm});
            skLineSegment(sketch, "E880", {"start": v(16.2, 0) * mm, "end": v(16.2, 0) * mm});
            skLineSegment(sketch, "E881", {"start": v(16.2, 0) * mm, "end": v(16.2, -483.8) * mm});
            skPoint(sketch, "E882.endSnap0", {"position": v(16.2, -692.25) * mm});
            skCircle(sketch, "E883", {"center": v(16.2, -483.8) * mm, "radius": 3.18 * mm});
            skCircle(sketch, "E884.0.1.0", {"center": v(16.2, -938.87) * mm, "radius": 3.18 * mm});
            skCircle(sketch, "E884.0.2.0", {"center": v(16.2, -1393.94) * mm, "radius": 3.18 * mm});
            skCircle(sketch, "E884.0.3.0", {"center": v(16.2, -1849) * mm, "radius": 3.18 * mm});
            skCircle(sketch, "E884.0.4.0", {"center": v(16.2, -2304.07) * mm, "radius": 3.18 * mm});
            skLineSegment(sketch, "E884.direction1", {"start": v(16.2, -483.8) * mm, "end": v(31.44, -483.8) * mm, "construction": true});
            skLineSegment(sketch, "E884.direction2", {"start": v(16.2, -483.8) * mm, "end": v(16.2, -938.87) * mm, "construction": true});
            skSolve(sketch);
        }
        {
            var Q0;
            Q0=makeQuery(id+"F2.imprint","IMPRINT",FACE,{"disambiguationData":[TD([[makeQuery(id+"F2.imprint","IMPRINT",EDGE,{"derivedFrom":sQuery(id+"F2.wireOp",EDGE,"E883")}),1.0]])]});
            var Q1;
            Q1=makeQuery(id+"F2.imprint","IMPRINT",FACE,{"disambiguationData":[TD([[makeQuery(id+"F2.imprint","IMPRINT",EDGE,{"derivedFrom":sQuery(id+"F2.wireOp",EDGE,"E884.0.1.0")}),1.0]])]});
            var Q2;
            Q2=makeQuery(id+"F2.imprint","IMPRINT",FACE,{"disambiguationData":[TD([[makeQuery(id+"F2.imprint","IMPRINT",EDGE,{"derivedFrom":sQuery(id+"F2.wireOp",EDGE,"E884.0.2.0")}),1.0]])]});
            var Q3;
            Q3=makeQuery(id+"F2.imprint","IMPRINT",FACE,{"disambiguationData":[TD([[makeQuery(id+"F2.imprint","IMPRINT",EDGE,{"derivedFrom":sQuery(id+"F2.wireOp",EDGE,"E884.0.3.0")}),1.0]])]});
            var Q4;
            Q4=makeQuery(id+"F2.imprint","IMPRINT",FACE,{"disambiguationData":[TD([[makeQuery(id+"F2.imprint","IMPRINT",EDGE,{"derivedFrom":sQuery(id+"F2.wireOp",EDGE,"E884.0.4.0")}),1.0]])]});
            extrude(context, id + "F3", {"entities" : qUnion([Q0, Q1, Q2, Q3, Q4]), "operationType" : NewBodyOperationType.REMOVE, "oppositeDirection" : true, "depth" : 5.46 * mm});
        }
        {
            var Q0;
            Q0=makeQuery(id+"F1.opExtrude","SWEPT_FACE",FACE,{"disambiguationData":[OSD([sQuery(id+"F0.wireOp",EDGE,"E733")])]});
            var sketch = newSketch(context, id + "F4", { "sketchPlane" : qUnion([Q0])});
            skLineSegment(sketch, "E885.bottom", {"start": v(-56.27, -2461.53) * mm, "end": v(92.9, -2461.53) * mm});
            skLineSegment(sketch, "E885.top", {"start": v(-56.27, -2331.98) * mm, "end": v(92.9, -2331.98) * mm});
            skLineSegment(sketch, "E885.left", {"start": v(-56.27, -2461.53) * mm, "end": v(-56.27, -2331.98) * mm});
            skLineSegment(sketch, "E885.right", {"start": v(92.9, -2461.53) * mm, "end": v(92.9, -2331.98) * mm});
            skSolve(sketch);
        }
        {
            var Q0;
            Q0=makeQuery(id+"F4.imprint","IMPRINT",FACE,{"disambiguationData":[TD([[makeQuery(id+"F4.imprint","IMPRINT",EDGE,{"derivedFrom":sQuery(id+"F4.wireOp",EDGE,"E885.bottom")}),1.0]])]});
            var Q1;
            {var subQ1=sQuery(id+"F0.wireOp",EDGE,"E733");var subQ6=makeQuery(id+"F1.opExtrude","CAP_EDGE",EDGE,{"disambiguationData":[OSD([subQ1])],"isStart":false});Q1=makeQuery(id+"F4.imprint","IMPRINT",FACE,{"disambiguationData":[TD([[makeQuery(id+"F4.imprint","IMPRINT",EDGE,{"derivedFrom":subQ6}),1.0]])]});}
            extrude(context, id + "F5", {"entities" : qUnion([Q0, Q1]), "operationType" : NewBodyOperationType.REMOVE, "endBound" : BoundingType.THROUGH_ALL, "oppositeDirection" : true, "depth" : 25.4 * mm});
        }
    });
